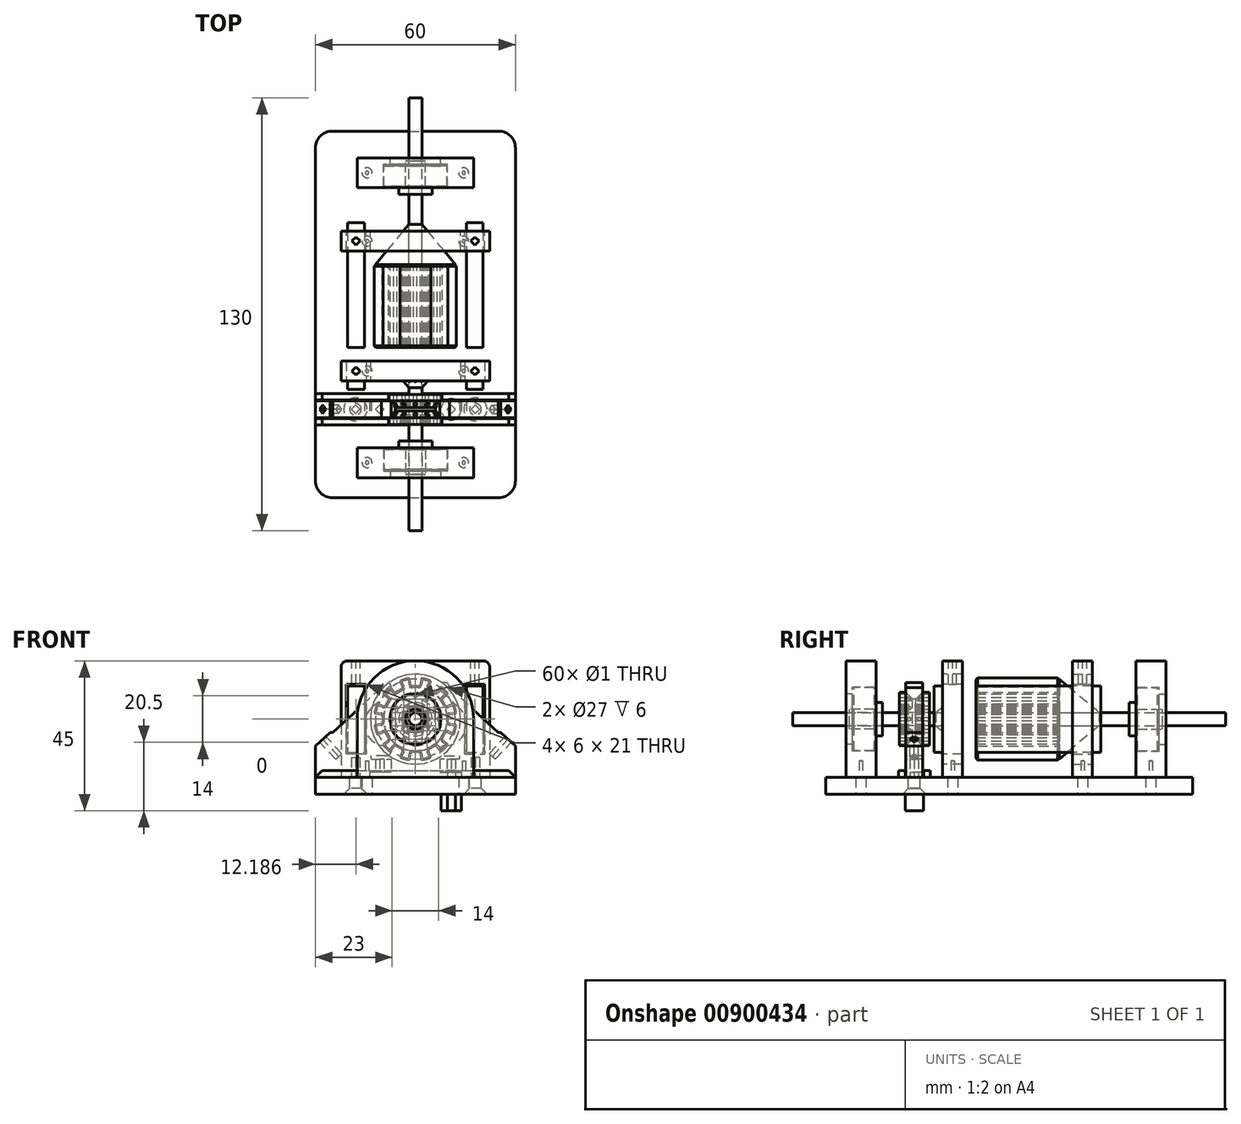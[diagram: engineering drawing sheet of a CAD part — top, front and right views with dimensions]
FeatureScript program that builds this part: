
annotation { "Feature Type Name" : "Feature", "Feature Type Description" : "" }
export const myFeature = defineFeature(function(context is Context, id is Id, definition is map)
    precondition{}
    {
        {
            var Q0;
            Q0=qCreatedBy(makeId("Front.planeOp"),FACE);
            var sketch = newSketch(context, id + "F0", { "sketchPlane" : qUnion([Q0])});
            skCircle(sketch, "E0", {"center": v(0, 0) * mm, "radius": 1.95 * mm});
            skSolve(sketch);
        }
        {
            var Q0;
            Q0=makeQuery(id+"F0.imprint","IMPRINT",FACE,{"disambiguationData":[TD([[makeQuery(id+"F0.imprint","IMPRINT",EDGE,{"derivedFrom":sQuery(id+"F0.wireOp",EDGE,"E0")}),1.0]])]});
            extrude(context, id + "F1", {"entities" : qUnion([Q0]), "depth" : 80 * mm, "offsetDistance" : 25 * mm, "hasSecondDirection" : true, "secondDirectionOppositeDirection" : true, "secondDirectionDepth" : 50 * mm});
        }
        {
            var Q0;
            Q0=qCreatedBy(makeId("Front.planeOp"),FACE);
            var sketch = newSketch(context, id + "F2", { "sketchPlane" : qUnion([Q0])});
            skCircle(sketch, "E1", {"center": v(0, 0) * mm, "radius": 15 * mm, "construction": true});
            skCircle(sketch, "E2", {"center": v(0, 0) * mm, "radius": 10 * mm, "construction": true});
            skLineSegment(sketch, "E3", {"start": v(0, 0) * mm, "end": v(15, 0) * mm, "construction": true});
            skLineSegment(sketch, "E4", {"start": v(0, 0) * mm, "end": v(9.91, 1.3) * mm, "construction": true});
            skLineSegment(sketch, "E5", {"start": v(0, 0) * mm, "end": v(9.91, -1.3) * mm, "construction": true});
            skLineSegment(sketch, "E6", {"start": v(11.89, 1.56) * mm, "end": v(10.35, 1.36) * mm});
            skLineSegment(sketch, "E7", {"start": v(9.91, 0.87) * mm, "end": v(9.91, -0.87) * mm});
            skLineSegment(sketch, "E8", {"start": v(10.35, -1.36) * mm, "end": v(11.89, -1.56) * mm});
            skPoint(sketch, "E9.visualSharp", {"position": v(9.91, 1.3) * mm});
            skArc(sketch, "E9.filletArc", {"start": v(10.35, 1.36) * mm, "mid": v(10.04, 1.2) * mm, "end": v(9.91, 0.87) * mm});
            skPoint(sketch, "E10.visualSharp", {"position": v(9.91, -1.3) * mm});
            skArc(sketch, "E10.filletArc", {"start": v(9.91, -0.87) * mm, "mid": v(10.04, -1.2) * mm, "end": v(10.35, -1.36) * mm});
            skArc(sketch, "E11.1.0", {"start": v(8.28, 6.35) * mm, "mid": v(8.1, 6.06) * mm, "end": v(8.15, 5.7) * mm});
            skLineSegment(sketch, "E11.1.1", {"start": v(9.51, 7.3) * mm, "end": v(8.28, 6.35) * mm});
            skLineSegment(sketch, "E11.1.2", {"start": v(8.15, 5.7) * mm, "end": v(9.02, 4.2) * mm});
            skArc(sketch, "E11.1.3", {"start": v(9.02, 4.2) * mm, "mid": v(9.3, 3.98) * mm, "end": v(9.64, 4) * mm});
            skLineSegment(sketch, "E11.1.4", {"start": v(9.64, 4) * mm, "end": v(11.08, 4.59) * mm});
            skArc(sketch, "E11.2.0", {"start": v(4, 9.64) * mm, "mid": v(3.98, 9.3) * mm, "end": v(4.2, 9.02) * mm});
            skLineSegment(sketch, "E11.2.1", {"start": v(4.59, 11.08) * mm, "end": v(4, 9.64) * mm});
            skLineSegment(sketch, "E11.2.2", {"start": v(4.2, 9.02) * mm, "end": v(5.7, 8.15) * mm});
            skArc(sketch, "E11.2.3", {"start": v(5.7, 8.15) * mm, "mid": v(6.06, 8.1) * mm, "end": v(6.35, 8.28) * mm});
            skLineSegment(sketch, "E11.2.4", {"start": v(6.35, 8.28) * mm, "end": v(7.3, 9.51) * mm});
            skLineSegment(sketch, "E12.4.3.0", {"start": v(-1.56, 11.89) * mm, "end": v(-1.36, 10.35) * mm});
            skLineSegment(sketch, "E12.7.3.0", {"start": v(-0.87, 9.91) * mm, "end": v(0.87, 9.91) * mm});
            skArc(sketch, "E12.10.3.0", {"start": v(0.87, 9.91) * mm, "mid": v(1.2, 10.04) * mm, "end": v(1.36, 10.35) * mm});
            skArc(sketch, "E12.13.3.0", {"start": v(-1.36, 10.35) * mm, "mid": v(-1.2, 10.04) * mm, "end": v(-0.87, 9.91) * mm});
            skLineSegment(sketch, "E12.14.3.0", {"start": v(1.36, 10.35) * mm, "end": v(1.56, 11.89) * mm});
            skLineSegment(sketch, "E12.4.4.0", {"start": v(-7.3, 9.51) * mm, "end": v(-6.35, 8.28) * mm});
            skLineSegment(sketch, "E12.7.4.0", {"start": v(-5.7, 8.15) * mm, "end": v(-4.2, 9.02) * mm});
            skArc(sketch, "E12.10.4.0", {"start": v(-4.2, 9.02) * mm, "mid": v(-3.98, 9.3) * mm, "end": v(-4, 9.64) * mm});
            skArc(sketch, "E12.13.4.0", {"start": v(-6.35, 8.28) * mm, "mid": v(-6.06, 8.1) * mm, "end": v(-5.7, 8.15) * mm});
            skLineSegment(sketch, "E12.14.4.0", {"start": v(-4, 9.64) * mm, "end": v(-4.59, 11.08) * mm});
            skLineSegment(sketch, "E12.4.5.0", {"start": v(-11.08, 4.59) * mm, "end": v(-9.64, 4) * mm});
            skLineSegment(sketch, "E12.7.5.0", {"start": v(-9.02, 4.2) * mm, "end": v(-8.15, 5.7) * mm});
            skArc(sketch, "E12.10.5.0", {"start": v(-8.15, 5.7) * mm, "mid": v(-8.1, 6.06) * mm, "end": v(-8.28, 6.35) * mm});
            skArc(sketch, "E12.13.5.0", {"start": v(-9.64, 4) * mm, "mid": v(-9.3, 3.98) * mm, "end": v(-9.02, 4.2) * mm});
            skLineSegment(sketch, "E12.14.5.0", {"start": v(-8.28, 6.35) * mm, "end": v(-9.51, 7.3) * mm});
            skLineSegment(sketch, "E12.4.6.0", {"start": v(-11.89, -1.56) * mm, "end": v(-10.35, -1.36) * mm});
            skLineSegment(sketch, "E12.7.6.0", {"start": v(-9.91, -0.87) * mm, "end": v(-9.91, 0.87) * mm});
            skArc(sketch, "E12.10.6.0", {"start": v(-9.91, 0.87) * mm, "mid": v(-10.04, 1.2) * mm, "end": v(-10.35, 1.36) * mm});
            skArc(sketch, "E12.13.6.0", {"start": v(-10.35, -1.36) * mm, "mid": v(-10.04, -1.2) * mm, "end": v(-9.91, -0.87) * mm});
            skLineSegment(sketch, "E12.14.6.0", {"start": v(-10.35, 1.36) * mm, "end": v(-11.89, 1.56) * mm});
            skLineSegment(sketch, "E12.4.7.0", {"start": v(-9.51, -7.3) * mm, "end": v(-8.28, -6.35) * mm});
            skLineSegment(sketch, "E12.7.7.0", {"start": v(-8.15, -5.7) * mm, "end": v(-9.02, -4.2) * mm});
            skArc(sketch, "E12.10.7.0", {"start": v(-9.02, -4.2) * mm, "mid": v(-9.3, -3.98) * mm, "end": v(-9.64, -4) * mm});
            skArc(sketch, "E12.13.7.0", {"start": v(-8.28, -6.35) * mm, "mid": v(-8.1, -6.06) * mm, "end": v(-8.15, -5.7) * mm});
            skLineSegment(sketch, "E12.14.7.0", {"start": v(-9.64, -4) * mm, "end": v(-11.08, -4.59) * mm});
            skLineSegment(sketch, "E12.4.8.0", {"start": v(-4.59, -11.08) * mm, "end": v(-4, -9.64) * mm});
            skLineSegment(sketch, "E12.7.8.0", {"start": v(-4.2, -9.02) * mm, "end": v(-5.7, -8.15) * mm});
            skArc(sketch, "E12.10.8.0", {"start": v(-5.7, -8.15) * mm, "mid": v(-6.06, -8.1) * mm, "end": v(-6.35, -8.28) * mm});
            skArc(sketch, "E12.13.8.0", {"start": v(-4, -9.64) * mm, "mid": v(-3.98, -9.3) * mm, "end": v(-4.2, -9.02) * mm});
            skLineSegment(sketch, "E12.14.8.0", {"start": v(-6.35, -8.28) * mm, "end": v(-7.3, -9.51) * mm});
            skLineSegment(sketch, "E12.4.9.0", {"start": v(1.56, -11.89) * mm, "end": v(1.36, -10.35) * mm});
            skLineSegment(sketch, "E12.7.9.0", {"start": v(0.87, -9.91) * mm, "end": v(-0.87, -9.91) * mm});
            skArc(sketch, "E12.10.9.0", {"start": v(-0.87, -9.91) * mm, "mid": v(-1.2, -10.04) * mm, "end": v(-1.36, -10.35) * mm});
            skArc(sketch, "E12.13.9.0", {"start": v(1.36, -10.35) * mm, "mid": v(1.2, -10.04) * mm, "end": v(0.87, -9.91) * mm});
            skLineSegment(sketch, "E12.14.9.0", {"start": v(-1.36, -10.35) * mm, "end": v(-1.56, -11.89) * mm});
            skLineSegment(sketch, "E12.4.10.0", {"start": v(7.3, -9.51) * mm, "end": v(6.35, -8.28) * mm});
            skLineSegment(sketch, "E12.7.10.0", {"start": v(5.7, -8.15) * mm, "end": v(4.2, -9.02) * mm});
            skArc(sketch, "E12.10.10.0", {"start": v(4.2, -9.02) * mm, "mid": v(3.98, -9.3) * mm, "end": v(4, -9.64) * mm});
            skArc(sketch, "E12.13.10.0", {"start": v(6.35, -8.28) * mm, "mid": v(6.06, -8.1) * mm, "end": v(5.7, -8.15) * mm});
            skLineSegment(sketch, "E12.14.10.0", {"start": v(4, -9.64) * mm, "end": v(4.59, -11.08) * mm});
            skLineSegment(sketch, "E12.4.11.0", {"start": v(11.08, -4.59) * mm, "end": v(9.64, -4) * mm});
            skLineSegment(sketch, "E12.7.11.0", {"start": v(9.02, -4.2) * mm, "end": v(8.15, -5.7) * mm});
            skArc(sketch, "E12.10.11.0", {"start": v(8.15, -5.7) * mm, "mid": v(8.1, -6.06) * mm, "end": v(8.28, -6.35) * mm});
            skArc(sketch, "E12.13.11.0", {"start": v(9.64, -4) * mm, "mid": v(9.3, -3.98) * mm, "end": v(9.02, -4.2) * mm});
            skLineSegment(sketch, "E12.14.11.0", {"start": v(8.28, -6.35) * mm, "end": v(9.51, -7.3) * mm});
            skArc(sketch, "E13", {"start": v(4.3, 11.74) * mm, "mid": v(3.24, 12.07) * mm, "end": v(2.15, 12.31) * mm});
            skArc(sketch, "E14.trimOffspring", {"start": v(9.6, 8.02) * mm, "mid": v(8.84, 8.84) * mm, "end": v(8.02, 9.6) * mm});
            skPoint(sketch, "E15.newPointA", {"position": v(7.61, 9.92) * mm});
            skArc(sketch, "E15.filletArc", {"start": v(8.02, 9.6) * mm, "mid": v(7.64, 9.7) * mm, "end": v(7.3, 9.51) * mm});
            skPoint(sketch, "E16.newPointB", {"position": v(9.92, 7.6) * mm});
            skArc(sketch, "E16.filletArc", {"start": v(9.51, 7.3) * mm, "mid": v(9.7, 7.64) * mm, "end": v(9.6, 8.02) * mm});
            skArc(sketch, "E17.trimOffspring", {"start": v(12.31, 2.15) * mm, "mid": v(12.07, 3.24) * mm, "end": v(11.74, 4.3) * mm});
            skArc(sketch, "E18.trimOffspring", {"start": v(11.74, -4.3) * mm, "mid": v(12.07, -3.24) * mm, "end": v(12.31, -2.15) * mm});
            skArc(sketch, "E19.trimOffspring", {"start": v(-2.15, 12.31) * mm, "mid": v(-3.24, 12.07) * mm, "end": v(-4.3, 11.74) * mm});
            skArc(sketch, "E20.trimOffspring", {"start": v(-8.02, 9.6) * mm, "mid": v(-8.84, 8.84) * mm, "end": v(-9.6, 8.02) * mm});
            skArc(sketch, "E21.trimOffspring", {"start": v(-11.74, 4.3) * mm, "mid": v(-12.07, 3.24) * mm, "end": v(-12.31, 2.15) * mm});
            skArc(sketch, "E22.trimOffspring", {"start": v(-12.31, -2.15) * mm, "mid": v(-12.07, -3.24) * mm, "end": v(-11.74, -4.3) * mm});
            skArc(sketch, "E23.trimOffspring", {"start": v(-9.6, -8.02) * mm, "mid": v(-8.84, -8.84) * mm, "end": v(-8.02, -9.6) * mm});
            skArc(sketch, "E24.trimOffspring", {"start": v(-4.3, -11.74) * mm, "mid": v(-3.24, -12.07) * mm, "end": v(-2.15, -12.31) * mm});
            skArc(sketch, "E25.trimOffspring", {"start": v(2.15, -12.31) * mm, "mid": v(3.24, -12.07) * mm, "end": v(4.3, -11.74) * mm});
            skArc(sketch, "E26.trimOffspring", {"start": v(8.02, -9.6) * mm, "mid": v(8.84, -8.84) * mm, "end": v(9.6, -8.02) * mm});
            skPoint(sketch, "E27.newPointB", {"position": v(4.78, 11.55) * mm});
            skArc(sketch, "E27.filletArc", {"start": v(4.59, 11.08) * mm, "mid": v(4.58, 11.47) * mm, "end": v(4.3, 11.74) * mm});
            skPoint(sketch, "E28.newPointB", {"position": v(1.63, 12.4) * mm});
            skArc(sketch, "E28.filletArc", {"start": v(2.15, 12.31) * mm, "mid": v(1.76, 12.22) * mm, "end": v(1.56, 11.89) * mm});
            skPoint(sketch, "E29.newPointB", {"position": v(-1.63, 12.4) * mm});
            skArc(sketch, "E29.filletArc", {"start": v(-1.56, 11.89) * mm, "mid": v(-1.76, 12.22) * mm, "end": v(-2.15, 12.31) * mm});
            skPoint(sketch, "E30.newPointB", {"position": v(-4.78, 11.55) * mm});
            skArc(sketch, "E30.filletArc", {"start": v(-4.3, 11.74) * mm, "mid": v(-4.58, 11.47) * mm, "end": v(-4.59, 11.08) * mm});
            skPoint(sketch, "E31.newPointB", {"position": v(-7.6, 9.92) * mm});
            skArc(sketch, "E31.filletArc", {"start": v(-7.3, 9.51) * mm, "mid": v(-7.64, 9.7) * mm, "end": v(-8.02, 9.6) * mm});
            skPoint(sketch, "E32.newPointB", {"position": v(-9.92, 7.61) * mm});
            skArc(sketch, "E32.filletArc", {"start": v(-9.6, 8.02) * mm, "mid": v(-9.7, 7.64) * mm, "end": v(-9.51, 7.3) * mm});
            skPoint(sketch, "E33.newPointB", {"position": v(-11.55, 4.78) * mm});
            skArc(sketch, "E33.filletArc", {"start": v(-11.08, 4.59) * mm, "mid": v(-11.47, 4.58) * mm, "end": v(-11.74, 4.3) * mm});
            skPoint(sketch, "E34.newPointB", {"position": v(-12.4, 1.63) * mm});
            skArc(sketch, "E34.filletArc", {"start": v(-12.31, 2.15) * mm, "mid": v(-12.22, 1.76) * mm, "end": v(-11.89, 1.56) * mm});
            skPoint(sketch, "E35.newPointA", {"position": v(-12.4, -1.63) * mm});
            skArc(sketch, "E35.filletArc", {"start": v(-11.89, -1.56) * mm, "mid": v(-12.22, -1.76) * mm, "end": v(-12.31, -2.15) * mm});
            skPoint(sketch, "E36.newPointA", {"position": v(-11.55, -4.78) * mm});
            skArc(sketch, "E36.filletArc", {"start": v(-11.74, -4.3) * mm, "mid": v(-11.47, -4.58) * mm, "end": v(-11.08, -4.59) * mm});
            skPoint(sketch, "E37.newPointA", {"position": v(-9.92, -7.6) * mm});
            skArc(sketch, "E37.filletArc", {"start": v(-9.51, -7.3) * mm, "mid": v(-9.7, -7.64) * mm, "end": v(-9.6, -8.02) * mm});
            skPoint(sketch, "E38.newPointA", {"position": v(-7.61, -9.92) * mm});
            skArc(sketch, "E38.filletArc", {"start": v(-8.02, -9.6) * mm, "mid": v(-7.64, -9.7) * mm, "end": v(-7.3, -9.51) * mm});
            skPoint(sketch, "E39.newPointA", {"position": v(-4.78, -11.55) * mm});
            skArc(sketch, "E39.filletArc", {"start": v(-4.59, -11.08) * mm, "mid": v(-4.58, -11.47) * mm, "end": v(-4.3, -11.74) * mm});
            skPoint(sketch, "E40.newPointA", {"position": v(-1.63, -12.4) * mm});
            skArc(sketch, "E40.filletArc", {"start": v(-2.15, -12.31) * mm, "mid": v(-1.76, -12.22) * mm, "end": v(-1.56, -11.89) * mm});
            skPoint(sketch, "E41.newPointA", {"position": v(1.63, -12.4) * mm});
            skArc(sketch, "E41.filletArc", {"start": v(1.56, -11.89) * mm, "mid": v(1.76, -12.22) * mm, "end": v(2.15, -12.31) * mm});
            skPoint(sketch, "E42.newPointA", {"position": v(4.78, -11.55) * mm});
            skArc(sketch, "E42.filletArc", {"start": v(4.3, -11.74) * mm, "mid": v(4.58, -11.47) * mm, "end": v(4.59, -11.08) * mm});
            skPoint(sketch, "E43.newPointA", {"position": v(7.6, -9.92) * mm});
            skArc(sketch, "E43.filletArc", {"start": v(7.3, -9.51) * mm, "mid": v(7.64, -9.7) * mm, "end": v(8.02, -9.6) * mm});
            skPoint(sketch, "E44.newPointA", {"position": v(9.92, -7.61) * mm});
            skArc(sketch, "E44.filletArc", {"start": v(9.6, -8.02) * mm, "mid": v(9.7, -7.64) * mm, "end": v(9.51, -7.3) * mm});
            skPoint(sketch, "E45.newPointB", {"position": v(11.55, -4.78) * mm});
            skArc(sketch, "E45.filletArc", {"start": v(11.08, -4.59) * mm, "mid": v(11.47, -4.58) * mm, "end": v(11.74, -4.3) * mm});
            skPoint(sketch, "E46.newPointA", {"position": v(12.4, -1.63) * mm});
            skArc(sketch, "E46.filletArc", {"start": v(12.31, -2.15) * mm, "mid": v(12.22, -1.76) * mm, "end": v(11.89, -1.56) * mm});
            skPoint(sketch, "E47.newPointA", {"position": v(12.4, 1.63) * mm});
            skArc(sketch, "E47.filletArc", {"start": v(11.89, 1.56) * mm, "mid": v(12.22, 1.76) * mm, "end": v(12.31, 2.15) * mm});
            skPoint(sketch, "E48.newPointB", {"position": v(11.55, 4.78) * mm});
            skArc(sketch, "E48.filletArc", {"start": v(11.74, 4.3) * mm, "mid": v(11.47, 4.58) * mm, "end": v(11.08, 4.59) * mm});
            skCircle(sketch, "E49", {"center": v(0, 0) * mm, "radius": 2 * mm});
            skPoint(sketch, "E50.centerSnap0", {"position": v(7.5, 0) * mm});
            skSolve(sketch);
        }
        {
            var Q0;
            Q0=makeQuery(id+"F2.imprint","IMPRINT",FACE,{"disambiguationData":[TD([[makeQuery(id+"F2.imprint","IMPRINT",EDGE,{"derivedFrom":sQuery(id+"F2.wireOp",EDGE,"E6")}),-1.0]])]});
            extrude(context, id + "F3", {"entities" : qUnion([Q0]), "depth" : 25 * mm, "offsetDistance" : 25 * mm});
        }
        {
            var Q0;
            Q0=makeQuery(id+"F3.opExtrude","CAP_FACE",FACE,{"disambiguationData":[OSD([sQuery(id+"F2.wireOp",EDGE,"E6"),sQuery(id+"F2.wireOp",EDGE,"E7"),sQuery(id+"F2.wireOp",EDGE,"E8"),sQuery(id+"F2.wireOp",EDGE,"E9.filletArc"),sQuery(id+"F2.wireOp",EDGE,"E10.filletArc"),sQuery(id+"F2.wireOp",EDGE,"E11.1.0"),sQuery(id+"F2.wireOp",EDGE,"E11.1.1"),sQuery(id+"F2.wireOp",EDGE,"E11.1.2"),sQuery(id+"F2.wireOp",EDGE,"E11.1.3"),sQuery(id+"F2.wireOp",EDGE,"E11.1.4"),sQuery(id+"F2.wireOp",EDGE,"E11.2.0"),sQuery(id+"F2.wireOp",EDGE,"E11.2.1"),sQuery(id+"F2.wireOp",EDGE,"E11.2.2"),sQuery(id+"F2.wireOp",EDGE,"E11.2.3"),sQuery(id+"F2.wireOp",EDGE,"E11.2.4"),sQuery(id+"F2.wireOp",EDGE,"E12.4.3.0"),sQuery(id+"F2.wireOp",EDGE,"E12.7.3.0"),sQuery(id+"F2.wireOp",EDGE,"E12.10.3.0"),sQuery(id+"F2.wireOp",EDGE,"E12.13.3.0"),sQuery(id+"F2.wireOp",EDGE,"E12.14.3.0"),sQuery(id+"F2.wireOp",EDGE,"E12.4.4.0"),sQuery(id+"F2.wireOp",EDGE,"E12.7.4.0"),sQuery(id+"F2.wireOp",EDGE,"E12.10.4.0"),sQuery(id+"F2.wireOp",EDGE,"E12.13.4.0"),sQuery(id+"F2.wireOp",EDGE,"E12.14.4.0"),sQuery(id+"F2.wireOp",EDGE,"E12.4.5.0"),sQuery(id+"F2.wireOp",EDGE,"E12.7.5.0"),sQuery(id+"F2.wireOp",EDGE,"E12.10.5.0"),sQuery(id+"F2.wireOp",EDGE,"E12.13.5.0"),sQuery(id+"F2.wireOp",EDGE,"E12.14.5.0"),sQuery(id+"F2.wireOp",EDGE,"E12.4.6.0"),sQuery(id+"F2.wireOp",EDGE,"E12.7.6.0"),sQuery(id+"F2.wireOp",EDGE,"E12.10.6.0"),sQuery(id+"F2.wireOp",EDGE,"E12.13.6.0"),sQuery(id+"F2.wireOp",EDGE,"E12.14.6.0"),sQuery(id+"F2.wireOp",EDGE,"E12.4.7.0"),sQuery(id+"F2.wireOp",EDGE,"E12.7.7.0"),sQuery(id+"F2.wireOp",EDGE,"E12.10.7.0"),sQuery(id+"F2.wireOp",EDGE,"E12.13.7.0"),sQuery(id+"F2.wireOp",EDGE,"E12.14.7.0"),sQuery(id+"F2.wireOp",EDGE,"E12.4.8.0"),sQuery(id+"F2.wireOp",EDGE,"E12.7.8.0"),sQuery(id+"F2.wireOp",EDGE,"E12.10.8.0"),sQuery(id+"F2.wireOp",EDGE,"E12.13.8.0"),sQuery(id+"F2.wireOp",EDGE,"E12.14.8.0"),sQuery(id+"F2.wireOp",EDGE,"E12.4.9.0"),sQuery(id+"F2.wireOp",EDGE,"E12.7.9.0"),sQuery(id+"F2.wireOp",EDGE,"E12.10.9.0"),sQuery(id+"F2.wireOp",EDGE,"E12.13.9.0"),sQuery(id+"F2.wireOp",EDGE,"E12.14.9.0"),sQuery(id+"F2.wireOp",EDGE,"E12.4.10.0"),sQuery(id+"F2.wireOp",EDGE,"E12.7.10.0"),sQuery(id+"F2.wireOp",EDGE,"E12.10.10.0"),sQuery(id+"F2.wireOp",EDGE,"E12.13.10.0"),sQuery(id+"F2.wireOp",EDGE,"E12.14.10.0"),sQuery(id+"F2.wireOp",EDGE,"E12.4.11.0"),sQuery(id+"F2.wireOp",EDGE,"E12.7.11.0"),sQuery(id+"F2.wireOp",EDGE,"E12.10.11.0"),sQuery(id+"F2.wireOp",EDGE,"E12.13.11.0"),sQuery(id+"F2.wireOp",EDGE,"E12.14.11.0"),sQuery(id+"F2.wireOp",EDGE,"E13"),sQuery(id+"F2.wireOp",EDGE,"E14.trimOffspring"),sQuery(id+"F2.wireOp",EDGE,"E15.filletArc"),sQuery(id+"F2.wireOp",EDGE,"E16.filletArc"),sQuery(id+"F2.wireOp",EDGE,"E17.trimOffspring"),sQuery(id+"F2.wireOp",EDGE,"E18.trimOffspring"),sQuery(id+"F2.wireOp",EDGE,"E19.trimOffspring"),sQuery(id+"F2.wireOp",EDGE,"E20.trimOffspring"),sQuery(id+"F2.wireOp",EDGE,"E21.trimOffspring"),sQuery(id+"F2.wireOp",EDGE,"E22.trimOffspring"),sQuery(id+"F2.wireOp",EDGE,"E23.trimOffspring"),sQuery(id+"F2.wireOp",EDGE,"E24.trimOffspring"),sQuery(id+"F2.wireOp",EDGE,"E25.trimOffspring"),sQuery(id+"F2.wireOp",EDGE,"E26.trimOffspring"),sQuery(id+"F2.wireOp",EDGE,"E27.filletArc"),sQuery(id+"F2.wireOp",EDGE,"E28.filletArc"),sQuery(id+"F2.wireOp",EDGE,"E29.filletArc"),sQuery(id+"F2.wireOp",EDGE,"E30.filletArc"),sQuery(id+"F2.wireOp",EDGE,"E31.filletArc"),sQuery(id+"F2.wireOp",EDGE,"E32.filletArc"),sQuery(id+"F2.wireOp",EDGE,"E33.filletArc"),sQuery(id+"F2.wireOp",EDGE,"E34.filletArc"),sQuery(id+"F2.wireOp",EDGE,"E35.filletArc"),sQuery(id+"F2.wireOp",EDGE,"E36.filletArc"),sQuery(id+"F2.wireOp",EDGE,"E37.filletArc"),sQuery(id+"F2.wireOp",EDGE,"E38.filletArc"),sQuery(id+"F2.wireOp",EDGE,"E39.filletArc"),sQuery(id+"F2.wireOp",EDGE,"E40.filletArc"),sQuery(id+"F2.wireOp",EDGE,"E41.filletArc"),sQuery(id+"F2.wireOp",EDGE,"E42.filletArc"),sQuery(id+"F2.wireOp",EDGE,"E43.filletArc"),sQuery(id+"F2.wireOp",EDGE,"E44.filletArc"),sQuery(id+"F2.wireOp",EDGE,"E45.filletArc"),sQuery(id+"F2.wireOp",EDGE,"E46.filletArc"),sQuery(id+"F2.wireOp",EDGE,"E47.filletArc"),sQuery(id+"F2.wireOp",EDGE,"E48.filletArc"),sQuery(id+"F2.wireOp",EDGE,"E49")])],"isStart":false});
            chamfer(context, id + "F4", {"entities" : qUnion([Q0]), "width" : 0.5 * mm, "tangentPropagation" : true});
        }
        {
            var Q0;
            Q0=makeQuery(id+"F3.opExtrude","CAP_FACE",FACE,{"disambiguationData":[OSD([sQuery(id+"F2.wireOp",EDGE,"E6"),sQuery(id+"F2.wireOp",EDGE,"E7"),sQuery(id+"F2.wireOp",EDGE,"E8"),sQuery(id+"F2.wireOp",EDGE,"E9.filletArc"),sQuery(id+"F2.wireOp",EDGE,"E10.filletArc"),sQuery(id+"F2.wireOp",EDGE,"E11.1.0"),sQuery(id+"F2.wireOp",EDGE,"E11.1.1"),sQuery(id+"F2.wireOp",EDGE,"E11.1.2"),sQuery(id+"F2.wireOp",EDGE,"E11.1.3"),sQuery(id+"F2.wireOp",EDGE,"E11.1.4"),sQuery(id+"F2.wireOp",EDGE,"E11.2.0"),sQuery(id+"F2.wireOp",EDGE,"E11.2.1"),sQuery(id+"F2.wireOp",EDGE,"E11.2.2"),sQuery(id+"F2.wireOp",EDGE,"E11.2.3"),sQuery(id+"F2.wireOp",EDGE,"E11.2.4"),sQuery(id+"F2.wireOp",EDGE,"E12.4.3.0"),sQuery(id+"F2.wireOp",EDGE,"E12.7.3.0"),sQuery(id+"F2.wireOp",EDGE,"E12.10.3.0"),sQuery(id+"F2.wireOp",EDGE,"E12.13.3.0"),sQuery(id+"F2.wireOp",EDGE,"E12.14.3.0"),sQuery(id+"F2.wireOp",EDGE,"E12.4.4.0"),sQuery(id+"F2.wireOp",EDGE,"E12.7.4.0"),sQuery(id+"F2.wireOp",EDGE,"E12.10.4.0"),sQuery(id+"F2.wireOp",EDGE,"E12.13.4.0"),sQuery(id+"F2.wireOp",EDGE,"E12.14.4.0"),sQuery(id+"F2.wireOp",EDGE,"E12.4.5.0"),sQuery(id+"F2.wireOp",EDGE,"E12.7.5.0"),sQuery(id+"F2.wireOp",EDGE,"E12.10.5.0"),sQuery(id+"F2.wireOp",EDGE,"E12.13.5.0"),sQuery(id+"F2.wireOp",EDGE,"E12.14.5.0"),sQuery(id+"F2.wireOp",EDGE,"E12.4.6.0"),sQuery(id+"F2.wireOp",EDGE,"E12.7.6.0"),sQuery(id+"F2.wireOp",EDGE,"E12.10.6.0"),sQuery(id+"F2.wireOp",EDGE,"E12.13.6.0"),sQuery(id+"F2.wireOp",EDGE,"E12.14.6.0"),sQuery(id+"F2.wireOp",EDGE,"E12.4.7.0"),sQuery(id+"F2.wireOp",EDGE,"E12.7.7.0"),sQuery(id+"F2.wireOp",EDGE,"E12.10.7.0"),sQuery(id+"F2.wireOp",EDGE,"E12.13.7.0"),sQuery(id+"F2.wireOp",EDGE,"E12.14.7.0"),sQuery(id+"F2.wireOp",EDGE,"E12.4.8.0"),sQuery(id+"F2.wireOp",EDGE,"E12.7.8.0"),sQuery(id+"F2.wireOp",EDGE,"E12.10.8.0"),sQuery(id+"F2.wireOp",EDGE,"E12.13.8.0"),sQuery(id+"F2.wireOp",EDGE,"E12.14.8.0"),sQuery(id+"F2.wireOp",EDGE,"E12.4.9.0"),sQuery(id+"F2.wireOp",EDGE,"E12.7.9.0"),sQuery(id+"F2.wireOp",EDGE,"E12.10.9.0"),sQuery(id+"F2.wireOp",EDGE,"E12.13.9.0"),sQuery(id+"F2.wireOp",EDGE,"E12.14.9.0"),sQuery(id+"F2.wireOp",EDGE,"E12.4.10.0"),sQuery(id+"F2.wireOp",EDGE,"E12.7.10.0"),sQuery(id+"F2.wireOp",EDGE,"E12.10.10.0"),sQuery(id+"F2.wireOp",EDGE,"E12.13.10.0"),sQuery(id+"F2.wireOp",EDGE,"E12.14.10.0"),sQuery(id+"F2.wireOp",EDGE,"E12.4.11.0"),sQuery(id+"F2.wireOp",EDGE,"E12.7.11.0"),sQuery(id+"F2.wireOp",EDGE,"E12.10.11.0"),sQuery(id+"F2.wireOp",EDGE,"E12.13.11.0"),sQuery(id+"F2.wireOp",EDGE,"E12.14.11.0"),sQuery(id+"F2.wireOp",EDGE,"E13"),sQuery(id+"F2.wireOp",EDGE,"E14.trimOffspring"),sQuery(id+"F2.wireOp",EDGE,"E15.filletArc"),sQuery(id+"F2.wireOp",EDGE,"E16.filletArc"),sQuery(id+"F2.wireOp",EDGE,"E17.trimOffspring"),sQuery(id+"F2.wireOp",EDGE,"E18.trimOffspring"),sQuery(id+"F2.wireOp",EDGE,"E19.trimOffspring"),sQuery(id+"F2.wireOp",EDGE,"E20.trimOffspring"),sQuery(id+"F2.wireOp",EDGE,"E21.trimOffspring"),sQuery(id+"F2.wireOp",EDGE,"E22.trimOffspring"),sQuery(id+"F2.wireOp",EDGE,"E23.trimOffspring"),sQuery(id+"F2.wireOp",EDGE,"E24.trimOffspring"),sQuery(id+"F2.wireOp",EDGE,"E25.trimOffspring"),sQuery(id+"F2.wireOp",EDGE,"E26.trimOffspring"),sQuery(id+"F2.wireOp",EDGE,"E27.filletArc"),sQuery(id+"F2.wireOp",EDGE,"E28.filletArc"),sQuery(id+"F2.wireOp",EDGE,"E29.filletArc"),sQuery(id+"F2.wireOp",EDGE,"E30.filletArc"),sQuery(id+"F2.wireOp",EDGE,"E31.filletArc"),sQuery(id+"F2.wireOp",EDGE,"E32.filletArc"),sQuery(id+"F2.wireOp",EDGE,"E33.filletArc"),sQuery(id+"F2.wireOp",EDGE,"E34.filletArc"),sQuery(id+"F2.wireOp",EDGE,"E35.filletArc"),sQuery(id+"F2.wireOp",EDGE,"E36.filletArc"),sQuery(id+"F2.wireOp",EDGE,"E37.filletArc"),sQuery(id+"F2.wireOp",EDGE,"E38.filletArc"),sQuery(id+"F2.wireOp",EDGE,"E39.filletArc"),sQuery(id+"F2.wireOp",EDGE,"E40.filletArc"),sQuery(id+"F2.wireOp",EDGE,"E41.filletArc"),sQuery(id+"F2.wireOp",EDGE,"E42.filletArc"),sQuery(id+"F2.wireOp",EDGE,"E43.filletArc"),sQuery(id+"F2.wireOp",EDGE,"E44.filletArc"),sQuery(id+"F2.wireOp",EDGE,"E45.filletArc"),sQuery(id+"F2.wireOp",EDGE,"E46.filletArc"),sQuery(id+"F2.wireOp",EDGE,"E47.filletArc"),sQuery(id+"F2.wireOp",EDGE,"E48.filletArc"),sQuery(id+"F2.wireOp",EDGE,"E49")])],"isStart":true});
            chamfer(context, id + "F5", {"entities" : qUnion([Q0]), "width" : 0.5 * mm, "tangentPropagation" : true});
        }
        {
            var Q0;
            Q0=qCreatedBy(makeId("Top.planeOp"),FACE);
            var sketch = newSketch(context, id + "F6", { "sketchPlane" : qUnion([Q0])});
            skLineSegment(sketch, "E51", {"start": v(2, 0) * mm, "end": v(12, 0) * mm});
            skLineSegment(sketch, "E52", {"start": v(12, 0) * mm, "end": v(2, 12) * mm});
            skLineSegment(sketch, "E53", {"start": v(2, 12) * mm, "end": v(2, 0) * mm});
            skLineSegment(sketch, "E54", {"start": v(0, 0) * mm, "end": v(-30, 0) * mm, "construction": true});
            skLineSegment(sketch, "E55", {"start": v(-30, -25) * mm, "end": v(0, -25) * mm, "construction": true});
            skLineSegment(sketch, "E56", {"start": v(-30, 0) * mm, "end": v(-30, -25) * mm, "construction": true});
            skLineSegment(sketch, "E57", {"start": v(-30, -12.5) * mm, "end": v(0, -12.5) * mm, "construction": true});
            skLineSegment(sketch, "E58.MirrorCS", {"start": v(2, -25) * mm, "end": v(12, -25) * mm});
            skLineSegment(sketch, "E59.MirrorCS", {"start": v(2, -37) * mm, "end": v(2, -25) * mm});
            skLineSegment(sketch, "E60.MirrorCS", {"start": v(12, -25) * mm, "end": v(2, -37) * mm});
            skLineSegment(sketch, "E61", {"start": v(0, 0) * mm, "end": v(0, -25) * mm, "construction": true});
            skSolve(sketch);
        }
        {
            var Q0;
            Q0=makeQuery(id+"F6.imprint","IMPRINT",FACE,{"disambiguationData":[TD([[makeQuery(id+"F6.imprint","IMPRINT",EDGE,{"derivedFrom":sQuery(id+"F6.wireOp",EDGE,"E51")}),1.0]])]});
            var Q1;
            Q1=makeQuery(id+"F6.imprint","IMPRINT",FACE,{"disambiguationData":[TD([[makeQuery(id+"F6.imprint","IMPRINT",EDGE,{"derivedFrom":sQuery(id+"F6.wireOp",EDGE,"E58.MirrorCS")}),-1.0]])]});
            var Q2;
            Q2=sQuery(id+"F6.wireOp",EDGE,"E61");
            revolve(context, id + "F7", {"surfaceOperationType" : NewSurfaceOperationType.NEW, "entities" : qUnion([Q0, Q1]), "axis" : qUnion([Q2]), "revolveType" : RevolveType.FULL});
        }
        {
            var Q0;
            Q0=qCreatedBy(makeId("Front.planeOp"),FACE);
            var sketch = newSketch(context, id + "F8", { "sketchPlane" : qUnion([Q0])});
            skCircle(sketch, "E62", {"center": v(7, 0) * mm, "radius": 0.5 * mm});
            skCircle(sketch, "E63", {"center": v(4, 0) * mm, "radius": 0.5 * mm});
            skCircle(sketch, "E64.1.0", {"center": v(3.46, 2) * mm, "radius": 0.5 * mm});
            skCircle(sketch, "E64.1.1", {"center": v(6.06, 3.5) * mm, "radius": 0.5 * mm});
            skCircle(sketch, "E64.2.0", {"center": v(2, 3.46) * mm, "radius": 0.5 * mm});
            skCircle(sketch, "E64.2.1", {"center": v(3.5, 6.06) * mm, "radius": 0.5 * mm});
            skPoint(sketch, "E64.center", {"position": v(0, 0) * mm});
            skCircle(sketch, "E65.1.3.0", {"center": v(0, 4) * mm, "radius": 0.5 * mm});
            skCircle(sketch, "E65.2.3.0", {"center": v(0, 7) * mm, "radius": 0.5 * mm});
            skCircle(sketch, "E65.1.4.0", {"center": v(-2, 3.46) * mm, "radius": 0.5 * mm});
            skCircle(sketch, "E65.2.4.0", {"center": v(-3.5, 6.06) * mm, "radius": 0.5 * mm});
            skCircle(sketch, "E65.1.5.0", {"center": v(-3.46, 2) * mm, "radius": 0.5 * mm});
            skCircle(sketch, "E65.2.5.0", {"center": v(-6.06, 3.5) * mm, "radius": 0.5 * mm});
            skCircle(sketch, "E65.1.6.0", {"center": v(-4, 0) * mm, "radius": 0.5 * mm});
            skCircle(sketch, "E65.2.6.0", {"center": v(-7, 0) * mm, "radius": 0.5 * mm});
            skCircle(sketch, "E65.1.7.0", {"center": v(-3.46, -2) * mm, "radius": 0.5 * mm});
            skCircle(sketch, "E65.2.7.0", {"center": v(-6.06, -3.5) * mm, "radius": 0.5 * mm});
            skCircle(sketch, "E65.1.8.0", {"center": v(-2, -3.46) * mm, "radius": 0.5 * mm});
            skCircle(sketch, "E65.2.8.0", {"center": v(-3.5, -6.06) * mm, "radius": 0.5 * mm});
            skCircle(sketch, "E65.1.9.0", {"center": v(0, -4) * mm, "radius": 0.5 * mm});
            skCircle(sketch, "E65.2.9.0", {"center": v(0, -7) * mm, "radius": 0.5 * mm});
            skCircle(sketch, "E65.1.10.0", {"center": v(2, -3.46) * mm, "radius": 0.5 * mm});
            skCircle(sketch, "E65.2.10.0", {"center": v(3.5, -6.06) * mm, "radius": 0.5 * mm});
            skCircle(sketch, "E65.1.11.0", {"center": v(3.46, -2) * mm, "radius": 0.5 * mm});
            skCircle(sketch, "E65.2.11.0", {"center": v(6.06, -3.5) * mm, "radius": 0.5 * mm});
            skSolve(sketch);
        }
        {
            var Q0;
            Q0=qCreatedBy(makeId("Top.planeOp"),FACE);
            var sketch = newSketch(context, id + "F9", { "sketchPlane" : qUnion([Q0])});
            skLineSegment(sketch, "E66", {"start": v(2, -39) * mm, "end": v(8, -39) * mm});
            skLineSegment(sketch, "E67", {"start": v(8, -39) * mm, "end": v(8, -41) * mm});
            skLineSegment(sketch, "E68", {"start": v(8, -41) * mm, "end": v(6, -43) * mm});
            skLineSegment(sketch, "E69", {"start": v(6, -43) * mm, "end": v(6, -44) * mm});
            skLineSegment(sketch, "E70", {"start": v(6, -44) * mm, "end": v(8, -46) * mm});
            skLineSegment(sketch, "E71", {"start": v(8, -46) * mm, "end": v(8, -48) * mm});
            skLineSegment(sketch, "E72", {"start": v(8, -48) * mm, "end": v(2, -48) * mm});
            skLineSegment(sketch, "E73", {"start": v(2, -48) * mm, "end": v(2, -39) * mm});
            skLineSegment(sketch, "E74", {"start": v(0, -53.33) * mm, "end": v(0, 0) * mm, "construction": true});
            skSolve(sketch);
        }
        {
            var Q0;
            Q0=makeQuery(id+"F9.imprint","IMPRINT",FACE,{"disambiguationData":[TD([[makeQuery(id+"F9.imprint","IMPRINT",EDGE,{"derivedFrom":sQuery(id+"F9.wireOp",EDGE,"E66")}),-1.0]])]});
            var Q1;
            Q1=sQuery(id+"F9.wireOp",EDGE,"E74");
            revolve(context, id + "F10", {"surfaceOperationType" : NewSurfaceOperationType.NEW, "entities" : qUnion([Q0]), "axis" : qUnion([Q1]), "revolveType" : RevolveType.FULL});
        }
        {
            var Q0;
            Q0=makeQuery(id+"F8.imprint","IMPRINT",FACE,{"disambiguationData":[TD([[makeQuery(id+"F8.imprint","IMPRINT",EDGE,{"derivedFrom":sQuery(id+"F8.wireOp",EDGE,"E65.2.3.0")}),1.0]])]});
            var Q1;
            Q1=makeQuery(id+"F8.imprint","IMPRINT",FACE,{"disambiguationData":[TD([[makeQuery(id+"F8.imprint","IMPRINT",EDGE,{"derivedFrom":sQuery(id+"F8.wireOp",EDGE,"E64.2.1")}),1.0]])]});
            var Q2;
            Q2=makeQuery(id+"F8.imprint","IMPRINT",FACE,{"disambiguationData":[TD([[makeQuery(id+"F8.imprint","IMPRINT",EDGE,{"derivedFrom":sQuery(id+"F8.wireOp",EDGE,"E64.1.1")}),1.0]])]});
            var Q3;
            Q3=makeQuery(id+"F8.imprint","IMPRINT",FACE,{"disambiguationData":[TD([[makeQuery(id+"F8.imprint","IMPRINT",EDGE,{"derivedFrom":sQuery(id+"F8.wireOp",EDGE,"E62")}),1.0]])]});
            var Q4;
            Q4=makeQuery(id+"F8.imprint","IMPRINT",FACE,{"disambiguationData":[TD([[makeQuery(id+"F8.imprint","IMPRINT",EDGE,{"derivedFrom":sQuery(id+"F8.wireOp",EDGE,"E65.2.11.0")}),1.0]])]});
            var Q5;
            Q5=makeQuery(id+"F8.imprint","IMPRINT",FACE,{"disambiguationData":[TD([[makeQuery(id+"F8.imprint","IMPRINT",EDGE,{"derivedFrom":sQuery(id+"F8.wireOp",EDGE,"E65.2.4.0")}),1.0]])]});
            var Q6;
            Q6=makeQuery(id+"F8.imprint","IMPRINT",FACE,{"disambiguationData":[TD([[makeQuery(id+"F8.imprint","IMPRINT",EDGE,{"derivedFrom":sQuery(id+"F8.wireOp",EDGE,"E65.1.10.0")}),1.0]])]});
            var Q7;
            Q7=makeQuery(id+"F8.imprint","IMPRINT",FACE,{"disambiguationData":[TD([[makeQuery(id+"F8.imprint","IMPRINT",EDGE,{"derivedFrom":sQuery(id+"F8.wireOp",EDGE,"E65.2.6.0")}),1.0]])]});
            var Q8;
            Q8=makeQuery(id+"F8.imprint","IMPRINT",FACE,{"disambiguationData":[TD([[makeQuery(id+"F8.imprint","IMPRINT",EDGE,{"derivedFrom":sQuery(id+"F8.wireOp",EDGE,"E65.2.7.0")}),1.0]])]});
            var Q9;
            Q9=makeQuery(id+"F8.imprint","IMPRINT",FACE,{"disambiguationData":[TD([[makeQuery(id+"F8.imprint","IMPRINT",EDGE,{"derivedFrom":sQuery(id+"F8.wireOp",EDGE,"E65.2.8.0")}),1.0]])]});
            var Q10;
            Q10=makeQuery(id+"F8.imprint","IMPRINT",FACE,{"disambiguationData":[TD([[makeQuery(id+"F8.imprint","IMPRINT",EDGE,{"derivedFrom":sQuery(id+"F8.wireOp",EDGE,"E64.1.0")}),1.0]])]});
            var Q11;
            Q11=makeQuery(id+"F8.imprint","IMPRINT",FACE,{"disambiguationData":[TD([[makeQuery(id+"F8.imprint","IMPRINT",EDGE,{"derivedFrom":sQuery(id+"F8.wireOp",EDGE,"E65.2.10.0")}),1.0]])]});
            var Q12;
            Q12=makeQuery(id+"F8.imprint","IMPRINT",FACE,{"disambiguationData":[TD([[makeQuery(id+"F8.imprint","IMPRINT",EDGE,{"derivedFrom":sQuery(id+"F8.wireOp",EDGE,"E65.1.11.0")}),1.0]])]});
            var Q13;
            Q13=makeQuery(id+"F8.imprint","IMPRINT",FACE,{"disambiguationData":[TD([[makeQuery(id+"F8.imprint","IMPRINT",EDGE,{"derivedFrom":sQuery(id+"F8.wireOp",EDGE,"E64.2.0")}),1.0]])]});
            var Q14;
            Q14=makeQuery(id+"F8.imprint","IMPRINT",FACE,{"disambiguationData":[TD([[makeQuery(id+"F8.imprint","IMPRINT",EDGE,{"derivedFrom":sQuery(id+"F8.wireOp",EDGE,"E65.1.6.0")}),1.0]])]});
            var Q15;
            Q15=makeQuery(id+"F8.imprint","IMPRINT",FACE,{"disambiguationData":[TD([[makeQuery(id+"F8.imprint","IMPRINT",EDGE,{"derivedFrom":sQuery(id+"F8.wireOp",EDGE,"E65.1.4.0")}),1.0]])]});
            var Q16;
            Q16=makeQuery(id+"F8.imprint","IMPRINT",FACE,{"disambiguationData":[TD([[makeQuery(id+"F8.imprint","IMPRINT",EDGE,{"derivedFrom":sQuery(id+"F8.wireOp",EDGE,"E65.1.5.0")}),1.0]])]});
            var Q17;
            Q17=makeQuery(id+"F8.imprint","IMPRINT",FACE,{"disambiguationData":[TD([[makeQuery(id+"F8.imprint","IMPRINT",EDGE,{"derivedFrom":sQuery(id+"F8.wireOp",EDGE,"E65.1.7.0")}),1.0]])]});
            var Q18;
            Q18=makeQuery(id+"F8.imprint","IMPRINT",FACE,{"disambiguationData":[TD([[makeQuery(id+"F8.imprint","IMPRINT",EDGE,{"derivedFrom":sQuery(id+"F8.wireOp",EDGE,"E65.1.9.0")}),1.0]])]});
            var Q19;
            Q19=makeQuery(id+"F8.imprint","IMPRINT",FACE,{"disambiguationData":[TD([[makeQuery(id+"F8.imprint","IMPRINT",EDGE,{"derivedFrom":sQuery(id+"F8.wireOp",EDGE,"E65.1.8.0")}),1.0]])]});
            var Q20;
            Q20=makeQuery(id+"F8.imprint","IMPRINT",FACE,{"disambiguationData":[TD([[makeQuery(id+"F8.imprint","IMPRINT",EDGE,{"derivedFrom":sQuery(id+"F8.wireOp",EDGE,"E65.2.9.0")}),1.0]])]});
            var Q21;
            Q21=makeQuery(id+"F8.imprint","IMPRINT",FACE,{"disambiguationData":[TD([[makeQuery(id+"F8.imprint","IMPRINT",EDGE,{"derivedFrom":sQuery(id+"F8.wireOp",EDGE,"E65.2.5.0")}),1.0]])]});
            var Q22;
            Q22=makeQuery(id+"F8.imprint","IMPRINT",FACE,{"disambiguationData":[TD([[makeQuery(id+"F8.imprint","IMPRINT",EDGE,{"derivedFrom":sQuery(id+"F8.wireOp",EDGE,"E63")}),1.0]])]});
            var Q23;
            Q23=makeQuery(id+"F8.imprint","IMPRINT",FACE,{"disambiguationData":[TD([[makeQuery(id+"F8.imprint","IMPRINT",EDGE,{"derivedFrom":sQuery(id+"F8.wireOp",EDGE,"E65.1.3.0")}),1.0]])]});
            extrude(context, id + "F11", {"entities" : qUnion([Q0, Q1, Q2, Q3, Q4, Q5, Q6, Q7, Q8, Q9, Q10, Q11, Q12, Q13, Q14, Q15, Q16, Q17, Q18, Q19, Q20, Q21, Q22, Q23]), "operationType" : NewBodyOperationType.REMOVE, "depth" : 50 * mm, "offsetDistance" : 25 * mm});
        }
        {
            var Q0;
            Q0=qCreatedBy(makeId("Top.planeOp"),FACE);
            var sketch = newSketch(context, id + "F12", { "sketchPlane" : qUnion([Q0])});
            skLineSegment(sketch, "E75", {"start": v(2, -53) * mm, "end": v(2, -63) * mm});
            skLineSegment(sketch, "E76", {"start": v(2, -63) * mm, "end": v(3, -63) * mm});
            skLineSegment(sketch, "E77", {"start": v(3, -63) * mm, "end": v(3, -55) * mm});
            skLineSegment(sketch, "E78", {"start": v(3, -55) * mm, "end": v(5, -55) * mm});
            skLineSegment(sketch, "E79", {"start": v(5, -55) * mm, "end": v(5, -53) * mm});
            skLineSegment(sketch, "E80", {"start": v(5, -53) * mm, "end": v(3, -53) * mm});
            skLineSegment(sketch, "E81", {"start": v(3, -53) * mm, "end": v(3, -53) * mm});
            skLineSegment(sketch, "E82", {"start": v(3, -53) * mm, "end": v(2, -53) * mm});
            skLineSegment(sketch, "E83", {"start": v(3, -53) * mm, "end": v(3, -55) * mm, "construction": true});
            skLineSegment(sketch, "E84.bottom", {"start": v(3, -55.5) * mm, "end": v(9.5, -55.5) * mm});
            skLineSegment(sketch, "E84.top", {"start": v(3, -61.5) * mm, "end": v(9.5, -61.5) * mm});
            skLineSegment(sketch, "E84.left", {"start": v(3, -55.5) * mm, "end": v(3, -61.5) * mm});
            skLineSegment(sketch, "E84.right", {"start": v(9.5, -55.5) * mm, "end": v(9.5, -61.5) * mm});
            skLineSegment(sketch, "E85.bottom", {"start": v(9.6, -55) * mm, "end": v(16.6, -55) * mm});
            skLineSegment(sketch, "E85.left", {"start": v(9.6, -55) * mm, "end": v(9.6, -62) * mm});
            skLineSegment(sketch, "E85.right", {"start": v(16.6, -55) * mm, "end": v(16.6, -64) * mm});
            skLineSegment(sketch, "E86", {"start": v(5, -55) * mm, "end": v(9.6, -55) * mm, "construction": true});
            skLineSegment(sketch, "E87.bottom", {"start": v(9.6, -62) * mm, "end": v(7.6, -62) * mm});
            skLineSegment(sketch, "E87.right", {"start": v(7.6, -62) * mm, "end": v(7.6, -64) * mm});
            skLineSegment(sketch, "E88", {"start": v(7.6, -64) * mm, "end": v(16.6, -64) * mm});
            skSolve(sketch);
        }
        {
            var Q0;
            Q0=makeQuery(id+"F12.imprint","IMPRINT",FACE,{"disambiguationData":[TD([[makeQuery(id+"F12.imprint","IMPRINT",EDGE,{"derivedFrom":sQuery(id+"F12.wireOp",EDGE,"E75")}),1.0]])]});
            var Q1;
            Q1=makeQuery(id+"F1.opExtrude","SWEPT_FACE",FACE,{"disambiguationData":[OSD([sQuery(id+"F0.wireOp",EDGE,"E0")])]});
            revolve(context, id + "F13", {"surfaceOperationType" : NewSurfaceOperationType.NEW, "entities" : qUnion([Q0]), "axis" : qUnion([Q1]), "revolveType" : RevolveType.FULL});
        }
        {
            var Q0;
            Q0=makeQuery(id+"F12.imprint","IMPRINT",FACE,{"disambiguationData":[TD([[makeQuery(id+"F12.imprint","IMPRINT",EDGE,{"derivedFrom":sQuery(id+"F12.wireOp",EDGE,"E84.bottom")}),-1.0]])]});
            var Q1;
            Q1=makeQuery(id+"F1.opExtrude","SWEPT_FACE",FACE,{"disambiguationData":[OSD([sQuery(id+"F0.wireOp",EDGE,"E0")])]});
            revolve(context, id + "F14", {"surfaceOperationType" : NewSurfaceOperationType.NEW, "entities" : qUnion([Q0]), "axis" : qUnion([Q1]), "revolveType" : RevolveType.FULL});
        }
        {
            var Q0;
            Q0=makeQuery(id+"F12.imprint","IMPRINT",FACE,{"disambiguationData":[TD([[makeQuery(id+"F12.imprint","IMPRINT",EDGE,{"derivedFrom":sQuery(id+"F12.wireOp",EDGE,"E85.bottom")}),-1.0]])]});
            var Q1;
            Q1=makeQuery(id+"F1.opExtrude","SWEPT_FACE",FACE,{"disambiguationData":[OSD([sQuery(id+"F0.wireOp",EDGE,"E0")])]});
            revolve(context, id + "F15", {"surfaceOperationType" : NewSurfaceOperationType.NEW, "entities" : qUnion([Q0]), "axis" : qUnion([Q1]), "revolveType" : RevolveType.FULL});
        }
        {
            var Q0;
            Q0=qCreatedBy(makeId("Front.planeOp"),FACE);
            cPlane(context, id + "F16", {"entities" : qUnion([Q0]), "cplaneType" : CPlaneType.OFFSET, "offset" : 16 * mm, "width" : 150 * mm, "height" : 150 * mm});
        }
        {
            var Q0;
            Q0=qCreatedBy(makeId("Front.planeOp"),FACE);
            var sketch = newSketch(context, id + "F17", { "sketchPlane" : qUnion([Q0])});
            skCircle(sketch, "E89", {"center": v(0, 0) * mm, "radius": 13.1 * mm});
            skArc(sketch, "E90", {"start": v(17.5, 0) * mm, "mid": v(0, 17.5) * mm, "end": v(-17.5, 0) * mm});
            skLineSegment(sketch, "E91", {"start": v(0, 0) * mm, "end": v(17.5, 0) * mm, "construction": true});
            skLineSegment(sketch, "E92", {"start": v(0, 0) * mm, "end": v(-17.5, 0) * mm, "construction": true});
            skLineSegment(sketch, "E93", {"start": v(17.5, 0) * mm, "end": v(17.5, -17.5) * mm});
            skLineSegment(sketch, "E94", {"start": v(17.5, -17.5) * mm, "end": v(-17.5, -17.5) * mm});
            skLineSegment(sketch, "E95", {"start": v(-17.5, 0) * mm, "end": v(-17.5, -17.5) * mm});
            skSolve(sketch);
        }
        {
            var Q0;
            Q0=makeQuery(id+"F17.imprint","IMPRINT",FACE,{"disambiguationData":[TD([[makeQuery(id+"F17.imprint","IMPRINT",EDGE,{"derivedFrom":sQuery(id+"F17.wireOp",EDGE,"E89")}),-1.0]])]});
            extrude(context, id + "F18", {"entities" : qUnion([Q0]), "operationType" : NewBodyOperationType.ADD, "depth" : 64 * mm, "offsetDistance" : 25 * mm, "hasSecondDirection" : true, "secondDirectionOppositeDirection" : false, "secondDirectionDepth" : 55 * mm});
        }
        {
            var Q0;
            Q0=makeQuery(id+"F13.opRevolve","SWEPT_BODY",BODY,{"disambiguationData":[OSD([sQuery(id+"F12.wireOp",EDGE,"E75"),sQuery(id+"F12.wireOp",EDGE,"E76"),sQuery(id+"F12.wireOp",EDGE,"E77"),sQuery(id+"F12.wireOp",EDGE,"E78"),sQuery(id+"F12.wireOp",EDGE,"E79"),sQuery(id+"F12.wireOp",EDGE,"E80"),sQuery(id+"F12.wireOp",EDGE,"E81"),sQuery(id+"F12.wireOp",EDGE,"E82")])]});
            var Q1;
            Q1=makeQuery(id+"F14.opRevolve","SWEPT_BODY",BODY,{"disambiguationData":[OSD([sQuery(id+"F12.wireOp",EDGE,"E84.bottom"),sQuery(id+"F12.wireOp",EDGE,"E84.top"),sQuery(id+"F12.wireOp",EDGE,"E84.left"),sQuery(id+"F12.wireOp",EDGE,"E84.right")])]});
            var Q2;
            Q2=makeQuery(id+"F15.opRevolve","SWEPT_BODY",BODY,{"disambiguationData":[OSD([sQuery(id+"F12.wireOp",EDGE,"E85.bottom"),sQuery(id+"F12.wireOp",EDGE,"E85.left"),sQuery(id+"F12.wireOp",EDGE,"E85.right"),sQuery(id+"F12.wireOp",EDGE,"E87.bottom"),sQuery(id+"F12.wireOp",EDGE,"E87.right"),sQuery(id+"F12.wireOp",EDGE,"E88")])]});
            var Q3;
            Q3=qCreatedBy(id+"F16.planeOp",FACE);
            mirror(context, id + "F19", {"entities" : qUnion([Q0, Q1, Q2]), "mirrorPlane" : qUnion([Q3])});
        }
        {
            var Q0;
            Q0=qCreatedBy(makeId("Top.planeOp"),FACE);
            var sketch = newSketch(context, id + "F20", { "sketchPlane" : qUnion([Q0])});
            skLineSegment(sketch, "E96.bottom", {"start": v(-30, 40) * mm, "end": v(30, 40) * mm});
            skLineSegment(sketch, "E96.top", {"start": v(-30, -70) * mm, "end": v(30, -70) * mm});
            skLineSegment(sketch, "E96.left", {"start": v(-30, 40) * mm, "end": v(-30, -70) * mm});
            skLineSegment(sketch, "E96.right", {"start": v(30, 40) * mm, "end": v(30, -70) * mm});
            skLineSegment(sketch, "E97", {"start": v(0, 40) * mm, "end": v(0, -70) * mm, "construction": true});
            skSolve(sketch);
        }
        {
            var Q0;
            Q0 = qSketchRegion(id + "F20", true);
            extrude(context, id + "F21", {"entities" : qUnion([Q0]), "oppositeDirection" : true, "depth" : 22.5 * mm, "offsetDistance" : 25 * mm, "hasSecondDirection" : true, "secondDirectionOppositeDirection" : true, "secondDirectionDepth" : 17.5 * mm});
        }
        {
            var Q0;
            Q0=makeQuery(id+"F21.opExtrude","CAP_FACE",FACE,{"disambiguationData":[OSD([sQuery(id+"F20.wireOp",EDGE,"E96.bottom"),sQuery(id+"F20.wireOp",EDGE,"E96.top"),sQuery(id+"F20.wireOp",EDGE,"E96.left"),sQuery(id+"F20.wireOp",EDGE,"E96.right")])],"isStart":true});
            var sketch = newSketch(context, id + "F22", { "sketchPlane" : qUnion([Q0])});
            skLineSegment(sketch, "E98", {"start": v(-30, 0) * mm, "end": v(30, 0) * mm, "construction": true});
            skLineSegment(sketch, "E99", {"start": v(-30, -25) * mm, "end": v(30, -25) * mm, "construction": true});
            skLineSegment(sketch, "E100.bottom", {"start": v(15.31, 12.5) * mm, "end": v(20.31, 12.5) * mm});
            skLineSegment(sketch, "E100.top", {"start": v(15.31, -37.5) * mm, "end": v(20.31, -37.5) * mm});
            skLineSegment(sketch, "E100.left", {"start": v(15.31, 12.5) * mm, "end": v(15.31, -37.5) * mm});
            skLineSegment(sketch, "E100.right", {"start": v(20.31, 12.5) * mm, "end": v(20.31, -37.5) * mm});
            skLineSegment(sketch, "E101", {"start": v(12.31, 0) * mm, "end": v(12.31, -25) * mm, "construction": true});
            skLineSegment(sketch, "E102", {"start": v(-30, -37.5) * mm, "end": v(30, -37.5) * mm, "construction": true});
            skLineSegment(sketch, "E103", {"start": v(-30, 12.5) * mm, "end": v(30, 12.5) * mm, "construction": true});
            skLineSegment(sketch, "E104", {"start": v(-30, 12.5) * mm, "end": v(-30, 0) * mm, "construction": true});
            skLineSegment(sketch, "E105", {"start": v(-30, -25) * mm, "end": v(-30, -37.5) * mm, "construction": true});
            skLineSegment(sketch, "E106", {"start": v(0, 12.5) * mm, "end": v(0, -37.5) * mm, "construction": true});
            skLineSegment(sketch, "E107.MirrorCS", {"start": v(-15.31, 12.5) * mm, "end": v(-20.31, 12.5) * mm});
            skLineSegment(sketch, "E108.MirrorCS", {"start": v(-15.31, -37.5) * mm, "end": v(-20.31, -37.5) * mm});
            skLineSegment(sketch, "E109.MirrorCS", {"start": v(-20.31, 12.5) * mm, "end": v(-20.31, -37.5) * mm});
            skLineSegment(sketch, "E110.MirrorCS", {"start": v(-15.31, 12.5) * mm, "end": v(-15.31, -37.5) * mm});
            skSolve(sketch);
        }
        {
            var Q0;
            Q0=makeQuery(id+"F22.imprint","IMPRINT",FACE,{"disambiguationData":[TD([[makeQuery(id+"F22.imprint","IMPRINT",EDGE,{"derivedFrom":sQuery(id+"F22.wireOp",EDGE,"E100.bottom")}),-1.0]])]});
            var Q1;
            {var subQ5=sQuery(id+"F22.wireOp",EDGE,"E107.MirrorCS");Q1=makeQuery(id+"F22.imprint","IMPRINT",FACE,{"disambiguationData":[TD([[makeQuery(id+"F22.imprint","IMPRINT",EDGE,{"derivedFrom":subQ5}),1.0]])]});}
            extrude(context, id + "F23", {"entities" : qUnion([Q0, Q1]), "depth" : 27.5 * mm, "offsetDistance" : 25 * mm, "hasSecondDirection" : true, "secondDirectionOppositeDirection" : false, "secondDirectionDepth" : 7.5 * mm});
        }
        {
            var Q0;
            Q0=makeQuery(id+"F22.imprint","IMPRINT",FACE,{"disambiguationData":[TD([[makeQuery(id+"F22.imprint","IMPRINT",EDGE,{"derivedFrom":sQuery(id+"F22.wireOp",EDGE,"E100.bottom")}),1.0]])]});
            var sketch = newSketch(context, id + "F24", { "sketchPlane" : qUnion([Q0])});
            skLineSegment(sketch, "E111.bottom", {"start": v(-22.31, -29) * mm, "end": v(22.31, -29) * mm});
            skLineSegment(sketch, "E111.top", {"start": v(-22.31, -35) * mm, "end": v(22.31, -35) * mm});
            skLineSegment(sketch, "E111.left", {"start": v(-22.31, -29) * mm, "end": v(-22.31, -35) * mm});
            skLineSegment(sketch, "E111.right", {"start": v(22.31, -29) * mm, "end": v(22.31, -35) * mm});
            skSolve(sketch);
        }
        {
            var Q0;
            {var subQ0=sQuery(id+"F24.wireOp",EDGE,"E111.left");Q0=makeQuery(id+"F24.imprint","IMPRINT",FACE,{"disambiguationData":[TD([[makeQuery(id+"F24.imprint","IMPRINT",EDGE,{"derivedFrom":subQ0}),1.0]])]});}
            var Q1;
            {var subQ0=sQuery(id+"F24.wireOp",EDGE,"E111.bottom");var subQ1=makeQuery(id+"F22.imprint","IMPRINT",EDGE,{"derivedFrom":sQuery(id+"F22.wireOp",EDGE,"E109.MirrorCS")});var subQ2=makeQuery(id+"F24.imprint","INTERSECT",VERTEX,{"derivedFrom":[subQ1,subQ0]});Q1=makeQuery(id+"F24.imprint","IMPRINT",FACE,{"disambiguationData":[TD([[makeQuery(id+"F24.imprint","IMPRINT",EDGE,{"disambiguationData":[TD([[subQ2,-1.0]])],"derivedFrom":subQ0}),-1.0]])]});}
            var Q2;
            {var subQ0=sQuery(id+"F24.wireOp",EDGE,"E111.bottom");var subQ1=makeQuery(id+"F22.imprint","IMPRINT",EDGE,{"derivedFrom":sQuery(id+"F22.wireOp",EDGE,"E110.MirrorCS")});var subQ2=makeQuery(id+"F24.imprint","INTERSECT",VERTEX,{"derivedFrom":[subQ1,subQ0]});Q2=makeQuery(id+"F24.imprint","IMPRINT",FACE,{"disambiguationData":[TD([[makeQuery(id+"F24.imprint","IMPRINT",EDGE,{"disambiguationData":[TD([[subQ2,-1.0]])],"derivedFrom":subQ0}),-1.0]])]});}
            var Q3;
            {var subQ0=sQuery(id+"F24.wireOp",EDGE,"E111.bottom");var subQ1=makeQuery(id+"F22.imprint","IMPRINT",EDGE,{"derivedFrom":sQuery(id+"F22.wireOp",EDGE,"E100.left")});var subQ2=makeQuery(id+"F24.imprint","INTERSECT",VERTEX,{"derivedFrom":[subQ1,subQ0]});Q3=makeQuery(id+"F24.imprint","IMPRINT",FACE,{"disambiguationData":[TD([[makeQuery(id+"F24.imprint","IMPRINT",EDGE,{"disambiguationData":[TD([[subQ2,-1.0]])],"derivedFrom":subQ0}),-1.0]])]});}
            var Q4;
            {var subQ0=sQuery(id+"F24.wireOp",EDGE,"E111.right");Q4=makeQuery(id+"F24.imprint","IMPRINT",FACE,{"disambiguationData":[TD([[makeQuery(id+"F24.imprint","IMPRINT",EDGE,{"derivedFrom":subQ0}),-1.0]])]});}
            extrude(context, id + "F25", {"entities" : qUnion([Q0, Q1, Q2, Q3, Q4]), "depth" : 35 * mm, "offsetDistance" : 25 * mm});
        }
        {
            var Q0;
            Q0=makeQuery(id+"F25.opExtrude","CAP_FACE",FACE,{"disambiguationData":[OSD([sQuery(id+"F24.wireOp",EDGE,"E111.bottom"),sQuery(id+"F24.wireOp",EDGE,"E111.top"),sQuery(id+"F24.wireOp",EDGE,"E111.left"),sQuery(id+"F24.wireOp",EDGE,"E111.right")])],"isStart":false});
            var sketch = newSketch(context, id + "F26", { "sketchPlane" : qUnion([Q0])});
            skLineSegment(sketch, "E112", {"start": v(-17.81, -37.5) * mm, "end": v(-17.81, -29) * mm, "construction": true});
            skLineSegment(sketch, "E113", {"start": v(-22.31, -32) * mm, "end": v(22.31, -32) * mm, "construction": true});
            skCircle(sketch, "E114.cCircle", {"center": v(-17.81, -32) * mm, "radius": 0.88 * mm, "construction": true});
            skLineSegment(sketch, "E114.0", {"start": v(-19.06, -32) * mm, "end": v(-17.81, -30.75) * mm});
            skLineSegment(sketch, "E114.1", {"start": v(-17.81, -30.75) * mm, "end": v(-16.56, -32) * mm});
            skLineSegment(sketch, "E114.2", {"start": v(-16.56, -32) * mm, "end": v(-17.81, -33.25) * mm});
            skLineSegment(sketch, "E114.3", {"start": v(-17.81, -33.25) * mm, "end": v(-19.06, -32) * mm});
            skPoint(sketch, "E114.0.midPoint", {"position": v(-18.44, -31.37) * mm});
            skSolve(sketch);
        }
        {
            var Q0;
            Q0=makeQuery(id+"F26.imprint","IMPRINT",FACE,{"disambiguationData":[TD([[makeQuery(id+"F26.imprint","IMPRINT",EDGE,{"derivedFrom":sQuery(id+"F26.wireOp",EDGE,"E114.0")}),-1.0]])]});
            extrude(context, id + "F27", {"entities" : qUnion([Q0]), "oppositeDirection" : true, "depth" : 10 * mm, "offsetDistance" : 25 * mm, "hasSecondDirection" : true, "secondDirectionOppositeDirection" : false, "secondDirectionDepth" : 5 * mm});
        }
        {
            var Q0;
            Q0=makeQuery(id+"F27.opExtrude","SWEPT_BODY",BODY,{"disambiguationData":[OSD([sQuery(id+"F26.wireOp",EDGE,"E114.0"),sQuery(id+"F26.wireOp",EDGE,"E114.1"),sQuery(id+"F26.wireOp",EDGE,"E114.2"),sQuery(id+"F26.wireOp",EDGE,"E114.3")])]});
            var Q1;
            Q1=qCreatedBy(makeId("Right.planeOp"),FACE);
            mirror(context, id + "F28", {"entities" : qUnion([Q0]), "mirrorPlane" : qUnion([Q1])});
        }
        {
            var Q0;
            Q0=makeQuery(id+"F27.opExtrude","SWEPT_BODY",BODY,{"disambiguationData":[OSD([sQuery(id+"F26.wireOp",EDGE,"E114.0"),sQuery(id+"F26.wireOp",EDGE,"E114.1"),sQuery(id+"F26.wireOp",EDGE,"E114.2"),sQuery(id+"F26.wireOp",EDGE,"E114.3")])]});
            var Q1;
            Q1=makeQuery(id+"F28.opPattern","COPY",BODY,{"derivedFrom":makeQuery(id+"F27.opExtrude","SWEPT_BODY",BODY,{"disambiguationData":[OSD([sQuery(id+"F26.wireOp",EDGE,"E114.0"),sQuery(id+"F26.wireOp",EDGE,"E114.1"),sQuery(id+"F26.wireOp",EDGE,"E114.2"),sQuery(id+"F26.wireOp",EDGE,"E114.3")])]}),"instanceName":"1"});
            var Q2;
            Q2=makeQuery(id+"F25.opExtrude","SWEPT_BODY",BODY,{"disambiguationData":[OSD([sQuery(id+"F24.wireOp",EDGE,"E111.bottom"),sQuery(id+"F24.wireOp",EDGE,"E111.top"),sQuery(id+"F24.wireOp",EDGE,"E111.left"),sQuery(id+"F24.wireOp",EDGE,"E111.right")])]});
            booleanBodies(context, id + "F29", {"operationType" : BooleanOperationType.SUBTRACTION, "tools" : qUnion([Q0, Q1]), "targets" : qUnion([Q2])});
        }
        {
            var Q0;
            Q0=makeQuery(id+"F25.opExtrude","SWEPT_FACE",FACE,{"disambiguationData":[OSD([sQuery(id+"F24.wireOp",EDGE,"E111.top")])]});
            var sketch = newSketch(context, id + "F30", { "sketchPlane" : qUnion([Q0])});
            skCircle(sketch, "E115", {"center": v(0, 0) * mm, "radius": 13.5 * mm});
            skLineSegment(sketch, "E116", {"start": v(-20.31, 10) * mm, "end": v(-20.31, -10) * mm, "construction": true});
            skLineSegment(sketch, "E117", {"start": v(-15.31, 10) * mm, "end": v(-15.31, -10) * mm, "construction": true});
            skLineSegment(sketch, "E118", {"start": v(-20.31, 10) * mm, "end": v(-15.31, 10) * mm, "construction": true});
            skLineSegment(sketch, "E119", {"start": v(-20.31, -10) * mm, "end": v(-15.31, -10) * mm, "construction": true});
            skLineSegment(sketch, "E120.0", {"start": v(-20.81, 10.5) * mm, "end": v(-14.81, 10.5) * mm});
            skLineSegment(sketch, "E120.1", {"start": v(-20.81, 10.5) * mm, "end": v(-20.81, -10.5) * mm});
            skLineSegment(sketch, "E120.2", {"start": v(-20.81, -10.5) * mm, "end": v(-14.81, -10.5) * mm});
            skLineSegment(sketch, "E120.3", {"start": v(-14.81, 10.5) * mm, "end": v(-14.81, -10.5) * mm});
            skLineSegment(sketch, "E121", {"start": v(0, 17.5) * mm, "end": v(0, -17.5) * mm, "construction": true});
            skLineSegment(sketch, "E122.MirrorCS", {"start": v(20.81, 10.5) * mm, "end": v(14.81, 10.5) * mm});
            skLineSegment(sketch, "E123.MirrorCS", {"start": v(14.81, 10.5) * mm, "end": v(14.81, -10.5) * mm});
            skLineSegment(sketch, "E124.MirrorCS", {"start": v(20.81, 10.5) * mm, "end": v(20.81, -10.5) * mm});
            skLineSegment(sketch, "E125.MirrorCS", {"start": v(20.81, -10.5) * mm, "end": v(14.81, -10.5) * mm});
            skSolve(sketch);
        }
        {
            var Q0;
            Q0=makeQuery(id+"F30.imprint","IMPRINT",FACE,{"disambiguationData":[TD([[makeQuery(id+"F30.imprint","IMPRINT",EDGE,{"derivedFrom":sQuery(id+"F30.wireOp",EDGE,"E115")}),1.0]])]});
            var Q1;
            Q1=makeQuery(id+"F30.imprint","IMPRINT",FACE,{"disambiguationData":[TD([[makeQuery(id+"F30.imprint","IMPRINT",EDGE,{"derivedFrom":sQuery(id+"F30.wireOp",EDGE,"E120.0")}),-1.0]])]});
            var Q2;
            Q2=makeQuery(id+"F30.imprint","IMPRINT",FACE,{"disambiguationData":[TD([[makeQuery(id+"F30.imprint","IMPRINT",EDGE,{"derivedFrom":sQuery(id+"F30.wireOp",EDGE,"E122.MirrorCS")}),1.0]])]});
            extrude(context, id + "F31", {"entities" : qUnion([Q0, Q1, Q2]), "operationType" : NewBodyOperationType.REMOVE, "oppositeDirection" : true, "depth" : 10 * mm, "offsetDistance" : 25 * mm});
        }
        {
            var Q0;
            Q0=makeQuery(id+"F23.opExtrude","SWEPT_FACE",FACE,{"disambiguationData":[OSD([sQuery(id+"F22.wireOp",EDGE,"E100.top")])]});
            var Q1;
            Q1=makeQuery(id+"F23.opExtrude","SWEPT_FACE",FACE,{"disambiguationData":[OSD([sQuery(id+"F22.wireOp",EDGE,"E107.MirrorCS")])]});
            cPlane(context, id + "F32", {"entities" : qUnion([Q0, Q1]), "cplaneType" : CPlaneType.MID_PLANE, "offset" : 25 * mm, "flipAlignment" : true, "width" : 150 * mm, "height" : 150 * mm});
        }
        {
            var Q0;
            Q0=makeQuery(id+"F25.opExtrude","CAP_EDGE",EDGE,{"disambiguationData":[OSD([sQuery(id+"F24.wireOp",EDGE,"E111.right")])],"isStart":false});
            var Q1;
            Q1=makeQuery(id+"F25.opExtrude","CAP_EDGE",EDGE,{"disambiguationData":[OSD([sQuery(id+"F24.wireOp",EDGE,"E111.left")])],"isStart":false});
            fillet(context, id + "F33", {"entities" : qUnion([Q0, Q1]), "radius" : 2 * mm, "tangentPropagation" : true, "allowEdgeOverflow" : false});
        }
        {
            var Q0;
            Q0=makeQuery(id+"F25.opExtrude","SWEPT_BODY",BODY,{"disambiguationData":[OSD([sQuery(id+"F24.wireOp",EDGE,"E111.bottom"),sQuery(id+"F24.wireOp",EDGE,"E111.top"),sQuery(id+"F24.wireOp",EDGE,"E111.left"),sQuery(id+"F24.wireOp",EDGE,"E111.right")])]});
            var Q1;
            Q1=qCreatedBy(id+"F32.planeOp",FACE);
            mirror(context, id + "F34", {"operationType" : NewBodyOperationType.ADD, "entities" : qUnion([Q0]), "mirrorPlane" : qUnion([Q1])});
        }
        {
            var Q0;
            Q0=makeQuery(id+"F21.opExtrude","CAP_FACE",FACE,{"disambiguationData":[OSD([sQuery(id+"F20.wireOp",EDGE,"E96.bottom"),sQuery(id+"F20.wireOp",EDGE,"E96.top"),sQuery(id+"F20.wireOp",EDGE,"E96.left"),sQuery(id+"F20.wireOp",EDGE,"E96.right")])],"isStart":false});
            var sketch = newSketch(context, id + "F35", { "sketchPlane" : qUnion([Q0])});
            skLineSegment(sketch, "E126", {"start": v(-30, 32) * mm, "end": v(74.63, 32) * mm, "construction": true});
            skLineSegment(sketch, "E127", {"start": v(-30, -7) * mm, "end": v(74.63, -7) * mm, "construction": true});
            skLineSegment(sketch, "E128", {"start": v(14.5, -40) * mm, "end": v(14.5, 70) * mm, "construction": true});
            skLineSegment(sketch, "E129", {"start": v(-14.5, -40) * mm, "end": v(-14.5, 70) * mm, "construction": true});
            skLineSegment(sketch, "E130", {"start": v(-30, -27.5) * mm, "end": v(17.5, -27.5) * mm, "construction": true});
            skLineSegment(sketch, "E131", {"start": v(17.5, 59.5) * mm, "end": v(-30, 59.5) * mm, "construction": true});
            skCircle(sketch, "E132", {"center": v(-14.5, 59.5) * mm, "radius": 1.5 * mm});
            skCircle(sketch, "E133", {"center": v(14.5, 59.5) * mm, "radius": 1.5 * mm});
            skCircle(sketch, "E134", {"center": v(14.5, -27.5) * mm, "radius": 1.5 * mm});
            skCircle(sketch, "E135", {"center": v(-14.5, -27.5) * mm, "radius": 1.5 * mm});
            skCircle(sketch, "E136", {"center": v(14.5, 59.5) * mm, "radius": 0.5 * mm});
            skCircle(sketch, "E137", {"center": v(-14.5, 59.5) * mm, "radius": 0.5 * mm});
            skCircle(sketch, "E138", {"center": v(14.5, -27.5) * mm, "radius": 0.5 * mm});
            skCircle(sketch, "E139", {"center": v(-14.5, -27.5) * mm, "radius": 0.5 * mm});
            skCircle(sketch, "E140", {"center": v(-14.5, 32) * mm, "radius": 1.5 * mm});
            skCircle(sketch, "E141", {"center": v(14.5, 32) * mm, "radius": 0.5 * mm});
            skCircle(sketch, "E142", {"center": v(14.5, 32) * mm, "radius": 1.5 * mm});
            skCircle(sketch, "E143", {"center": v(-14.5, 32) * mm, "radius": 0.5 * mm});
            skCircle(sketch, "E144", {"center": v(14.5, -7) * mm, "radius": 0.5 * mm});
            skCircle(sketch, "E145", {"center": v(14.5, -7) * mm, "radius": 1.5 * mm});
            skCircle(sketch, "E146", {"center": v(-14.5, -7) * mm, "radius": 0.5 * mm});
            skCircle(sketch, "E147", {"center": v(-14.5, -7) * mm, "radius": 1.5 * mm});
            skSolve(sketch);
        }
        {
            var Q0;
            Q0=makeQuery(id+"F35.imprint","IMPRINT",FACE,{"disambiguationData":[TD([[makeQuery(id+"F35.imprint","IMPRINT",EDGE,{"derivedFrom":sQuery(id+"F35.wireOp",EDGE,"E132")}),1.0]])]});
            var Q1;
            Q1=makeQuery(id+"F35.imprint","IMPRINT",FACE,{"disambiguationData":[TD([[makeQuery(id+"F35.imprint","IMPRINT",EDGE,{"derivedFrom":sQuery(id+"F35.wireOp",EDGE,"E137")}),1.0]])]});
            var Q2;
            Q2=makeQuery(id+"F35.imprint","IMPRINT",FACE,{"disambiguationData":[TD([[makeQuery(id+"F35.imprint","IMPRINT",EDGE,{"derivedFrom":sQuery(id+"F35.wireOp",EDGE,"E136")}),1.0]])]});
            var Q3;
            Q3=makeQuery(id+"F35.imprint","IMPRINT",FACE,{"disambiguationData":[TD([[makeQuery(id+"F35.imprint","IMPRINT",EDGE,{"derivedFrom":sQuery(id+"F35.wireOp",EDGE,"E133")}),1.0]])]});
            var Q4;
            Q4=makeQuery(id+"F35.imprint","IMPRINT",FACE,{"disambiguationData":[TD([[makeQuery(id+"F35.imprint","IMPRINT",EDGE,{"derivedFrom":sQuery(id+"F35.wireOp",EDGE,"PFyNPDqs-Ep8R-HGao-31Ur-gI6ej4vQ4cxJ")}),1.0]])]});
            var Q5;
            Q5=makeQuery(id+"F35.imprint","IMPRINT",FACE,{"disambiguationData":[TD([[makeQuery(id+"F35.imprint","IMPRINT",EDGE,{"derivedFrom":sQuery(id+"F35.wireOp",EDGE,"Kp0F8KkM-gTSG-8IrS-7Ek4-cIwRPN5PFipR")}),1.0]])]});
            var Q6;
            Q6=makeQuery(id+"F35.imprint","IMPRINT",FACE,{"disambiguationData":[TD([[makeQuery(id+"F35.imprint","IMPRINT",EDGE,{"derivedFrom":sQuery(id+"F35.wireOp",EDGE,"OavnT1iM-PWWg-e2RI-Cgqf-CRE9zpLMibSG")}),1.0]])]});
            var Q7;
            Q7=makeQuery(id+"F35.imprint","IMPRINT",FACE,{"disambiguationData":[TD([[makeQuery(id+"F35.imprint","IMPRINT",EDGE,{"derivedFrom":sQuery(id+"F35.wireOp",EDGE,"6iWuaM59-P9UH-9INN-MEdt-I3GYd4iT0KjY")}),1.0]])]});
            var Q8;
            Q8=makeQuery(id+"F35.imprint","IMPRINT",FACE,{"disambiguationData":[TD([[makeQuery(id+"F35.imprint","IMPRINT",EDGE,{"derivedFrom":sQuery(id+"F35.wireOp",EDGE,"GS8uUdpl-7a4f-zSQ8-zMdr-q3VKJ9zmA7Z2")}),1.0]])]});
            var Q9;
            Q9=makeQuery(id+"F35.imprint","IMPRINT",FACE,{"disambiguationData":[TD([[makeQuery(id+"F35.imprint","IMPRINT",EDGE,{"derivedFrom":sQuery(id+"F35.wireOp",EDGE,"F0IPPkhX-6PCt-gYH3-62Ki-m6P0bRLTlL1H")}),1.0]])]});
            var Q10;
            Q10=makeQuery(id+"F35.imprint","IMPRINT",FACE,{"disambiguationData":[TD([[makeQuery(id+"F35.imprint","IMPRINT",EDGE,{"derivedFrom":sQuery(id+"F35.wireOp",EDGE,"SXbGrNF4-FH9E-IirH-lWky-iFOXS6nttWAW")}),1.0]])]});
            var Q11;
            Q11=makeQuery(id+"F35.imprint","IMPRINT",FACE,{"disambiguationData":[TD([[makeQuery(id+"F35.imprint","IMPRINT",EDGE,{"derivedFrom":sQuery(id+"F35.wireOp",EDGE,"XRTzMnL4-Fk8b-kX3F-CXxC-4Bn30n7xDRgZ")}),1.0]])]});
            var Q12;
            Q12=makeQuery(id+"F35.imprint","IMPRINT",FACE,{"disambiguationData":[TD([[makeQuery(id+"F35.imprint","IMPRINT",EDGE,{"derivedFrom":sQuery(id+"F35.wireOp",EDGE,"E138")}),1.0]])]});
            var Q13;
            Q13=makeQuery(id+"F35.imprint","IMPRINT",FACE,{"disambiguationData":[TD([[makeQuery(id+"F35.imprint","IMPRINT",EDGE,{"derivedFrom":sQuery(id+"F35.wireOp",EDGE,"E134")}),1.0]])]});
            var Q14;
            Q14=makeQuery(id+"F35.imprint","IMPRINT",FACE,{"disambiguationData":[TD([[makeQuery(id+"F35.imprint","IMPRINT",EDGE,{"derivedFrom":sQuery(id+"F35.wireOp",EDGE,"E139")}),1.0]])]});
            var Q15;
            Q15=makeQuery(id+"F35.imprint","IMPRINT",FACE,{"disambiguationData":[TD([[makeQuery(id+"F35.imprint","IMPRINT",EDGE,{"derivedFrom":sQuery(id+"F35.wireOp",EDGE,"E135")}),1.0]])]});
            var Q16;
            Q16=makeQuery(id+"F35.imprint","IMPRINT",FACE,{"disambiguationData":[TD([[makeQuery(id+"F35.imprint","IMPRINT",EDGE,{"derivedFrom":sQuery(id+"F35.wireOp",EDGE,"E141")}),-1.0]])]});
            var Q17;
            Q17=makeQuery(id+"F35.imprint","IMPRINT",FACE,{"disambiguationData":[TD([[makeQuery(id+"F35.imprint","IMPRINT",EDGE,{"derivedFrom":sQuery(id+"F35.wireOp",EDGE,"E141")}),1.0]])]});
            var Q18;
            Q18=makeQuery(id+"F35.imprint","IMPRINT",FACE,{"disambiguationData":[TD([[makeQuery(id+"F35.imprint","IMPRINT",EDGE,{"derivedFrom":sQuery(id+"F35.wireOp",EDGE,"E140")}),1.0]])]});
            var Q19;
            Q19=makeQuery(id+"F35.imprint","IMPRINT",FACE,{"disambiguationData":[TD([[makeQuery(id+"F35.imprint","IMPRINT",EDGE,{"derivedFrom":sQuery(id+"F35.wireOp",EDGE,"E143")}),1.0]])]});
            var Q20;
            Q20=makeQuery(id+"F35.imprint","IMPRINT",FACE,{"disambiguationData":[TD([[makeQuery(id+"F35.imprint","IMPRINT",EDGE,{"derivedFrom":sQuery(id+"F35.wireOp",EDGE,"E144")}),-1.0]])]});
            var Q21;
            Q21=makeQuery(id+"F35.imprint","IMPRINT",FACE,{"disambiguationData":[TD([[makeQuery(id+"F35.imprint","IMPRINT",EDGE,{"derivedFrom":sQuery(id+"F35.wireOp",EDGE,"E144")}),1.0]])]});
            var Q22;
            Q22=makeQuery(id+"F35.imprint","IMPRINT",FACE,{"disambiguationData":[TD([[makeQuery(id+"F35.imprint","IMPRINT",EDGE,{"derivedFrom":sQuery(id+"F35.wireOp",EDGE,"E146")}),1.0]])]});
            var Q23;
            Q23=makeQuery(id+"F35.imprint","IMPRINT",FACE,{"disambiguationData":[TD([[makeQuery(id+"F35.imprint","IMPRINT",EDGE,{"derivedFrom":sQuery(id+"F35.wireOp",EDGE,"E146")}),-1.0]])]});
            extrude(context, id + "F36", {"entities" : qUnion([Q0, Q1, Q2, Q3, Q4, Q5, Q6, Q7, Q8, Q9, Q10, Q11, Q12, Q13, Q14, Q15, Q16, Q17, Q18, Q19, Q20, Q21, Q22, Q23]), "operationType" : NewBodyOperationType.REMOVE, "oppositeDirection" : true, "depth" : 5 * mm, "offsetDistance" : 25 * mm});
        }
        {
            var Q0;
            Q0=makeQuery(id+"F35.imprint","IMPRINT",FACE,{"disambiguationData":[TD([[makeQuery(id+"F35.imprint","IMPRINT",EDGE,{"derivedFrom":sQuery(id+"F35.wireOp",EDGE,"E137")}),1.0]])]});
            var Q1;
            Q1=makeQuery(id+"F35.imprint","IMPRINT",FACE,{"disambiguationData":[TD([[makeQuery(id+"F35.imprint","IMPRINT",EDGE,{"derivedFrom":sQuery(id+"F35.wireOp",EDGE,"E136")}),1.0]])]});
            var Q2;
            Q2=makeQuery(id+"F35.imprint","IMPRINT",FACE,{"disambiguationData":[TD([[makeQuery(id+"F35.imprint","IMPRINT",EDGE,{"derivedFrom":sQuery(id+"F35.wireOp",EDGE,"Kp0F8KkM-gTSG-8IrS-7Ek4-cIwRPN5PFipR")}),1.0]])]});
            var Q3;
            Q3=makeQuery(id+"F35.imprint","IMPRINT",FACE,{"disambiguationData":[TD([[makeQuery(id+"F35.imprint","IMPRINT",EDGE,{"derivedFrom":sQuery(id+"F35.wireOp",EDGE,"OavnT1iM-PWWg-e2RI-Cgqf-CRE9zpLMibSG")}),1.0]])]});
            var Q4;
            Q4=makeQuery(id+"F35.imprint","IMPRINT",FACE,{"disambiguationData":[TD([[makeQuery(id+"F35.imprint","IMPRINT",EDGE,{"derivedFrom":sQuery(id+"F35.wireOp",EDGE,"SXbGrNF4-FH9E-IirH-lWky-iFOXS6nttWAW")}),1.0]])]});
            var Q5;
            Q5=makeQuery(id+"F35.imprint","IMPRINT",FACE,{"disambiguationData":[TD([[makeQuery(id+"F35.imprint","IMPRINT",EDGE,{"derivedFrom":sQuery(id+"F35.wireOp",EDGE,"GS8uUdpl-7a4f-zSQ8-zMdr-q3VKJ9zmA7Z2")}),1.0]])]});
            var Q6;
            Q6=makeQuery(id+"F35.imprint","IMPRINT",FACE,{"disambiguationData":[TD([[makeQuery(id+"F35.imprint","IMPRINT",EDGE,{"derivedFrom":sQuery(id+"F35.wireOp",EDGE,"E139")}),1.0]])]});
            var Q7;
            Q7=makeQuery(id+"F35.imprint","IMPRINT",FACE,{"disambiguationData":[TD([[makeQuery(id+"F35.imprint","IMPRINT",EDGE,{"derivedFrom":sQuery(id+"F35.wireOp",EDGE,"E138")}),1.0]])]});
            var Q8;
            Q8=makeQuery(id+"F35.imprint","IMPRINT",FACE,{"disambiguationData":[TD([[makeQuery(id+"F35.imprint","IMPRINT",EDGE,{"derivedFrom":sQuery(id+"F35.wireOp",EDGE,"E141")}),1.0]])]});
            var Q9;
            Q9=makeQuery(id+"F35.imprint","IMPRINT",FACE,{"disambiguationData":[TD([[makeQuery(id+"F35.imprint","IMPRINT",EDGE,{"derivedFrom":sQuery(id+"F35.wireOp",EDGE,"E143")}),1.0]])]});
            var Q10;
            Q10=makeQuery(id+"F35.imprint","IMPRINT",FACE,{"disambiguationData":[TD([[makeQuery(id+"F35.imprint","IMPRINT",EDGE,{"derivedFrom":sQuery(id+"F35.wireOp",EDGE,"E144")}),1.0]])]});
            var Q11;
            Q11=makeQuery(id+"F35.imprint","IMPRINT",FACE,{"disambiguationData":[TD([[makeQuery(id+"F35.imprint","IMPRINT",EDGE,{"derivedFrom":sQuery(id+"F35.wireOp",EDGE,"E146")}),1.0]])]});
            extrude(context, id + "F37", {"entities" : qUnion([Q0, Q1, Q2, Q3, Q4, Q5, Q6, Q7, Q8, Q9, Q10, Q11]), "operationType" : NewBodyOperationType.REMOVE, "oppositeDirection" : true, "depth" : 10 * mm, "offsetDistance" : 25 * mm});
        }
        {
            var Q0;
            Q0=makeQuery(id+"F21.opExtrude","SWEPT_EDGE",EDGE,{"disambiguationData":[OSD([sQuery(id+"F20.wireOp",EDGE,"E96.top"),sQuery(id+"F20.wireOp",EDGE,"E96.left")])]});
            var Q1;
            Q1=makeQuery(id+"F21.opExtrude","SWEPT_EDGE",EDGE,{"disambiguationData":[OSD([sQuery(id+"F20.wireOp",EDGE,"E96.top"),sQuery(id+"F20.wireOp",EDGE,"E96.right")])]});
            var Q2;
            Q2=makeQuery(id+"F21.opExtrude","SWEPT_EDGE",EDGE,{"disambiguationData":[OSD([sQuery(id+"F20.wireOp",EDGE,"E96.bottom"),sQuery(id+"F20.wireOp",EDGE,"E96.right")])]});
            var Q3;
            Q3=makeQuery(id+"F21.opExtrude","SWEPT_EDGE",EDGE,{"disambiguationData":[OSD([sQuery(id+"F20.wireOp",EDGE,"E96.bottom"),sQuery(id+"F20.wireOp",EDGE,"E96.left")])]});
            fillet(context, id + "F38", {"entities" : qUnion([Q0, Q1, Q2, Q3]), "radius" : 5 * mm, "tangentPropagation" : true, "allowEdgeOverflow" : false});
        }
        {
            var Q0;
            Q0=makeQuery(id+"F10.opRevolve","SWEPT_FACE",FACE,{"disambiguationData":[OSD([sQuery(id+"F9.wireOp",EDGE,"E72")])]});
            var sketch = newSketch(context, id + "F39", { "sketchPlane" : qUnion([Q0])});
            skLineSegment(sketch, "E148", {"start": v(7.25, 14.68) * mm, "end": v(7.25, -16) * mm, "construction": true});
            skLineSegment(sketch, "E149", {"start": v(-22.31, 8) * mm, "end": v(30, 8) * mm, "construction": true});
            skLineSegment(sketch, "E150", {"start": v(-22.31, -8) * mm, "end": v(8.75, -8) * mm, "construction": true});
            skArc(sketch, "E151", {"start": v(10.25, 9.47) * mm, "mid": v(8.16, 10.88) * mm, "end": v(7.73, 8.4) * mm});
            skLineSegment(sketch, "E152", {"start": v(13.75, -17.5) * mm, "end": v(30, -17.5) * mm});
            skLineSegment(sketch, "E153", {"start": v(30, -17.5) * mm, "end": v(30, -8.11) * mm});
            skLineSegment(sketch, "E154", {"start": v(25.6, -4.04) * mm, "end": v(24.86, -4.04) * mm});
            skLineSegment(sketch, "E155", {"start": v(25.6, -4.04) * mm, "end": v(9.77, 10.6) * mm, "construction": true});
            skArc(sketch, "E156", {"start": v(8.75, -8) * mm, "mid": v(7.25, -9.5) * mm, "end": v(8.75, -11) * mm});
            skLineSegment(sketch, "E157", {"start": v(7.25, -11) * mm, "end": v(8.75, -11) * mm, "construction": true});
            skLineSegment(sketch, "E158", {"start": v(13.25, -12) * mm, "end": v(7.25, -12) * mm});
            skLineSegment(sketch, "E159", {"start": v(7.25, -12) * mm, "end": v(7.25, -16) * mm});
            skLineSegment(sketch, "E160", {"start": v(8.75, -11) * mm, "end": v(13.25, -11) * mm});
            skLineSegment(sketch, "E161", {"start": v(10.25, 9.47) * mm, "end": v(24.86, -4.04) * mm});
            skLineSegment(sketch, "E162", {"start": v(7.73, 8.4) * mm, "end": v(13.2, 3.35) * mm});
            skLineSegment(sketch, "E163", {"start": v(8.75, -8) * mm, "end": v(8.75, -8) * mm});
            skArc(sketch, "E164.filletArc", {"start": v(8.75, -8) * mm, "mid": v(14.84, -3.84) * mm, "end": v(13.2, 3.35) * mm});
            skLineSegment(sketch, "E165", {"start": v(17.52, 3.43) * mm, "end": v(24.86, -3.36) * mm, "construction": true});
            skLineSegment(sketch, "E166", {"start": v(24.86, -3.36) * mm, "end": v(28.46, 0.53) * mm, "construction": true});
            skLineSegment(sketch, "E167", {"start": v(28.46, 0.53) * mm, "end": v(21.12, 7.32) * mm, "construction": true});
            skLineSegment(sketch, "E168", {"start": v(21.12, 7.32) * mm, "end": v(17.52, 3.43) * mm, "construction": true});
            skLineSegment(sketch, "E169", {"start": v(13.25, -12) * mm, "end": v(13.25, -11) * mm});
            skPoint(sketch, "E170.visualSharp", {"position": v(25.6, -4.04) * mm});
            skLineSegment(sketch, "E171", {"start": v(25.6, -4.04) * mm, "end": v(30, -8.11) * mm});
            skLineSegment(sketch, "E172", {"start": v(28.9, -7.1) * mm, "end": v(24.82, -11.5) * mm, "construction": true});
            skLineSegment(sketch, "E173", {"start": v(26.7, -5.06) * mm, "end": v(22.62, -9.46) * mm, "construction": true});
            skLineSegment(sketch, "E174", {"start": v(22.62, -9.46) * mm, "end": v(24.82, -11.5) * mm, "construction": true});
            skLineSegment(sketch, "E175", {"start": v(12.25, -12) * mm, "end": v(12.25, -17.5) * mm, "construction": true});
            skLineSegment(sketch, "E176", {"start": v(9.25, -12) * mm, "end": v(9.25, -17.5) * mm, "construction": true});
            skLineSegment(sketch, "E177", {"start": v(7.25, -16) * mm, "end": v(13.75, -16) * mm});
            skLineSegment(sketch, "E178", {"start": v(13.75, -16) * mm, "end": v(13.75, -17.5) * mm});
            skLineSegment(sketch, "E179", {"start": v(18, -9.5) * mm, "end": v(18, -17.5) * mm, "construction": true});
            skLineSegment(sketch, "E180", {"start": v(19.5, -9.5) * mm, "end": v(19.5, -17.5) * mm, "construction": true});
            skLineSegment(sketch, "E181", {"start": v(16.5, -9.5) * mm, "end": v(16.5, -17.5) * mm, "construction": true});
            skLineSegment(sketch, "E182", {"start": v(16.5, -9.5) * mm, "end": v(19.5, -9.5) * mm, "construction": true});
            skSolve(sketch);
        }
        {
            var Q0;
            Q0=makeQuery(id+"F39.imprint","IMPRINT",FACE,{"disambiguationData":[TD([[makeQuery(id+"F39.imprint","IMPRINT",EDGE,{"derivedFrom":sQuery(id+"F39.wireOp",EDGE,"E151")}),1.0]])]});
            extrude(context, id + "F40", {"entities" : qUnion([Q0]), "oppositeDirection" : true, "depth" : 7 * mm, "offsetDistance" : 25 * mm, "hasSecondDirection" : true, "secondDirectionOppositeDirection" : true, "secondDirectionDepth" : 2 * mm});
        }
        {
            var Q0;
            Q0=makeQuery(id+"F40.opExtrude","SWEPT_FACE",FACE,{"disambiguationData":[OSD([sQuery(id+"F39.wireOp",EDGE,"E171")])]});
            var sketch = newSketch(context, id + "F41", { "sketchPlane" : qUnion([Q0])});
            skLineSegment(sketch, "E183", {"start": v(24.53, -46) * mm, "end": v(24.53, -41) * mm, "construction": true});
            skLineSegment(sketch, "E184", {"start": v(23.03, -48) * mm, "end": v(26.03, -48) * mm, "construction": true});
            skLineSegment(sketch, "E185", {"start": v(24.53, -48) * mm, "end": v(24.53, -46) * mm, "construction": true});
            skCircle(sketch, "E186.cCircle", {"center": v(24.53, -43.5) * mm, "radius": 0.88 * mm, "construction": true});
            skLineSegment(sketch, "E186.0", {"start": v(23.28, -43.5) * mm, "end": v(24.53, -42.25) * mm});
            skLineSegment(sketch, "E186.1", {"start": v(24.53, -42.25) * mm, "end": v(25.78, -43.5) * mm});
            skLineSegment(sketch, "E186.2", {"start": v(25.78, -43.5) * mm, "end": v(24.53, -44.75) * mm});
            skLineSegment(sketch, "E186.3", {"start": v(24.53, -44.75) * mm, "end": v(23.28, -43.5) * mm});
            skPoint(sketch, "E186.0.midPoint", {"position": v(23.9, -42.88) * mm});
            skLineSegment(sketch, "E187", {"start": v(24.53, -43.5) * mm, "end": v(23.28, -43.5) * mm, "construction": true});
            skSolve(sketch);
        }
        {
            var Q0;
            Q0=makeQuery(id+"F41.imprint","IMPRINT",FACE,{"disambiguationData":[TD([[makeQuery(id+"F41.imprint","IMPRINT",EDGE,{"derivedFrom":sQuery(id+"F41.wireOp",EDGE,"E186.0")}),-1.0]])]});
            extrude(context, id + "F42", {"entities" : qUnion([Q0]), "operationType" : NewBodyOperationType.REMOVE, "oppositeDirection" : true, "depth" : 7 * mm, "offsetDistance" : 25 * mm});
        }
        {
            var Q0;
            Q0=makeQuery(id+"F40.opExtrude","SWEPT_FACE",FACE,{"disambiguationData":[OSD([sQuery(id+"F39.wireOp",EDGE,"E177")])]});
            var sketch = newSketch(context, id + "F43", { "sketchPlane" : qUnion([Q0])});
            skLineSegment(sketch, "E188", {"start": v(10.75, 46) * mm, "end": v(10.75, 41) * mm, "construction": true});
            skLineSegment(sketch, "E189", {"start": v(12.25, 48) * mm, "end": v(9.25, 48) * mm, "construction": true});
            skLineSegment(sketch, "E190", {"start": v(10.75, 48) * mm, "end": v(10.75, 46) * mm, "construction": true});
            skCircle(sketch, "E191.cCircle", {"center": v(10.75, 43.5) * mm, "radius": 0.88 * mm, "construction": true});
            skLineSegment(sketch, "E191.0", {"start": v(12, 43.5) * mm, "end": v(10.75, 42.25) * mm});
            skLineSegment(sketch, "E191.1", {"start": v(10.75, 42.25) * mm, "end": v(9.5, 43.5) * mm});
            skLineSegment(sketch, "E191.2", {"start": v(9.5, 43.5) * mm, "end": v(10.75, 44.75) * mm});
            skLineSegment(sketch, "E191.3", {"start": v(10.75, 44.75) * mm, "end": v(12, 43.5) * mm});
            skPoint(sketch, "E191.0.midPoint", {"position": v(11.38, 42.88) * mm});
            skSolve(sketch);
        }
        {
            var Q0;
            Q0=makeQuery(id+"F43.imprint","IMPRINT",FACE,{"disambiguationData":[TD([[makeQuery(id+"F43.imprint","IMPRINT",EDGE,{"derivedFrom":sQuery(id+"F43.wireOp",EDGE,"E191.0")}),-1.0]])]});
            extrude(context, id + "F44", {"entities" : qUnion([Q0]), "operationType" : NewBodyOperationType.REMOVE, "oppositeDirection" : true, "depth" : 4.5 * mm, "offsetDistance" : 25 * mm});
        }
        {
            var Q0;
            Q0=makeQuery(id+"F21.opExtrude","CAP_FACE",FACE,{"disambiguationData":[OSD([sQuery(id+"F20.wireOp",EDGE,"E96.bottom"),sQuery(id+"F20.wireOp",EDGE,"E96.top"),sQuery(id+"F20.wireOp",EDGE,"E96.left"),sQuery(id+"F20.wireOp",EDGE,"E96.right")])],"isStart":true});
            var sketch = newSketch(context, id + "F45", { "sketchPlane" : qUnion([Q0])});
            skLineSegment(sketch, "E192", {"start": v(18, -48) * mm, "end": v(18, -46) * mm, "construction": true});
            skLineSegment(sketch, "E193", {"start": v(18, -46) * mm, "end": v(18, -41) * mm, "construction": true});
            skCircle(sketch, "E194.cCircle", {"center": v(18, -43.5) * mm, "radius": 0.88 * mm, "construction": true});
            skLineSegment(sketch, "E194.0", {"start": v(19.25, -43.5) * mm, "end": v(18, -44.75) * mm});
            skLineSegment(sketch, "E194.1", {"start": v(18, -44.75) * mm, "end": v(16.75, -43.5) * mm});
            skLineSegment(sketch, "E194.2", {"start": v(16.75, -43.5) * mm, "end": v(18, -42.25) * mm});
            skLineSegment(sketch, "E194.3", {"start": v(18, -42.25) * mm, "end": v(19.25, -43.5) * mm});
            skPoint(sketch, "E194.0.midPoint", {"position": v(18.62, -44.12) * mm});
            skCircle(sketch, "E195", {"center": v(18, -43.5) * mm, "radius": 1.75 * mm});
            skCircle(sketch, "E196", {"center": v(10.75, -43.5) * mm, "radius": 3 * mm});
            skLineSegment(sketch, "E197.bottom", {"start": v(-30, -46.25) * mm, "end": v(30, -46.25) * mm});
            skLineSegment(sketch, "E197.top", {"start": v(-30, -48.25) * mm, "end": v(30, -48.25) * mm});
            skLineSegment(sketch, "E197.left", {"start": v(-30, -46.25) * mm, "end": v(-30, -48.25) * mm});
            skLineSegment(sketch, "E197.right", {"start": v(30, -46.25) * mm, "end": v(30, -48.25) * mm});
            skLineSegment(sketch, "E198.bottom", {"start": v(-30, -38.75) * mm, "end": v(30, -38.75) * mm});
            skLineSegment(sketch, "E198.top", {"start": v(-30, -40.75) * mm, "end": v(30, -40.75) * mm});
            skLineSegment(sketch, "E198.left", {"start": v(-30, -38.75) * mm, "end": v(-30, -40.75) * mm});
            skLineSegment(sketch, "E198.right", {"start": v(30, -38.75) * mm, "end": v(30, -40.75) * mm});
            skSolve(sketch);
        }
        {
            var Q0;
            Q0=makeQuery(id+"F45.imprint","IMPRINT",FACE,{"disambiguationData":[TD([[makeQuery(id+"F45.imprint","IMPRINT",EDGE,{"derivedFrom":sQuery(id+"F45.wireOp",EDGE,"E196")}),1.0]])]});
            var Q1;
            {var subQ0=sQuery(id+"F45.wireOp",EDGE,"E197.bottom");var subQ1=sQuery(id+"F45.wireOp",EDGE,"E196");var subQ2=makeQuery(id+"F45.imprint","INTERSECT",VERTEX,{"disambiguationData":[OD(0.0)],"derivedFrom":[subQ1,subQ0]});Q1=makeQuery(id+"F45.imprint","IMPRINT",FACE,{"disambiguationData":[TD([[makeQuery(id+"F45.imprint","IMPRINT",EDGE,{"disambiguationData":[TD([[subQ2,-1.0]])],"derivedFrom":subQ1}),1.0]])]});}
            var Q2;
            {var subQ0=sQuery(id+"F45.wireOp",EDGE,"E198.top");var subQ1=sQuery(id+"F45.wireOp",EDGE,"E196");var subQ2=makeQuery(id+"F45.imprint","INTERSECT",VERTEX,{"disambiguationData":[OD(0.0)],"derivedFrom":[subQ1,subQ0]});Q2=makeQuery(id+"F45.imprint","IMPRINT",FACE,{"disambiguationData":[TD([[makeQuery(id+"F45.imprint","IMPRINT",EDGE,{"disambiguationData":[TD([[subQ2,1.0]])],"derivedFrom":subQ1}),1.0]])]});}
            extrude(context, id + "F46", {"entities" : qUnion([Q0, Q1, Q2]), "oppositeDirection" : true, "depth" : 10 * mm, "offsetDistance" : 25 * mm});
        }
        {
            var Q0;
            Q0=makeQuery(id+"F45.imprint","IMPRINT",FACE,{"disambiguationData":[TD([[makeQuery(id+"F45.imprint","IMPRINT",EDGE,{"derivedFrom":sQuery(id+"F45.wireOp",EDGE,"E194.0")}),1.0]])]});
            var Q1;
            Q1=makeQuery(id+"F45.imprint","IMPRINT",FACE,{"disambiguationData":[TD([[makeQuery(id+"F45.imprint","IMPRINT",EDGE,{"derivedFrom":sQuery(id+"F45.wireOp",EDGE,"E194.0")}),-1.0]])]});
            extrude(context, id + "F47", {"entities" : qUnion([Q0, Q1]), "oppositeDirection" : true, "depth" : 10 * mm, "offsetDistance" : 25 * mm, "hasSecondDirection" : true, "secondDirectionOppositeDirection" : false, "secondDirectionDepth" : 5 * mm});
        }
        {
            var Q0;
            Q0=makeQuery(id+"F45.imprint","IMPRINT",FACE,{"disambiguationData":[TD([[makeQuery(id+"F45.imprint","IMPRINT",EDGE,{"derivedFrom":sQuery(id+"F45.wireOp",EDGE,"E194.0")}),-1.0]])]});
            extrude(context, id + "F48", {"entities" : qUnion([Q0]), "operationType" : NewBodyOperationType.REMOVE, "depth" : 6 * mm, "offsetDistance" : 25 * mm});
        }
        {
            var Q0;
            Q0=makeQuery(id+"F40.opExtrude","SWEPT_BODY",BODY,{"disambiguationData":[OSD([sQuery(id+"F39.wireOp",EDGE,"E151"),sQuery(id+"F39.wireOp",EDGE,"E152"),sQuery(id+"F39.wireOp",EDGE,"E153"),sQuery(id+"F39.wireOp",EDGE,"E154"),sQuery(id+"F39.wireOp",EDGE,"E156"),sQuery(id+"F39.wireOp",EDGE,"E158"),sQuery(id+"F39.wireOp",EDGE,"E159"),sQuery(id+"F39.wireOp",EDGE,"E160"),sQuery(id+"F39.wireOp",EDGE,"E161"),sQuery(id+"F39.wireOp",EDGE,"E162"),sQuery(id+"F39.wireOp",EDGE,"E164.filletArc"),sQuery(id+"F39.wireOp",EDGE,"E169"),sQuery(id+"F39.wireOp",EDGE,"E171"),sQuery(id+"F39.wireOp",EDGE,"E177"),sQuery(id+"F39.wireOp",EDGE,"E178")])]});
            var Q1;
            Q1=qCreatedBy(makeId("Right.planeOp"),FACE);
            mirror(context, id + "F49", {"entities" : qUnion([Q0]), "mirrorPlane" : qUnion([Q1])});
        }
        {
            var Q0;
            Q0=makeQuery(id+"F45.imprint","IMPRINT",FACE,{"disambiguationData":[TD([[makeQuery(id+"F45.imprint","IMPRINT",EDGE,{"derivedFrom":sQuery(id+"F45.wireOp",EDGE,"E198.bottom")}),-1.0]])]});
            var Q1;
            Q1=makeQuery(id+"F45.imprint","IMPRINT",FACE,{"disambiguationData":[TD([[makeQuery(id+"F45.imprint","IMPRINT",EDGE,{"derivedFrom":sQuery(id+"F45.wireOp",EDGE,"E197.top")}),1.0]])]});
            extrude(context, id + "F50", {"entities" : qUnion([Q0, Q1]), "operationType" : NewBodyOperationType.ADD, "depth" : 2 * mm, "offsetDistance" : 25 * mm});
        }
        {
            var Q0;
            Q0=makeQuery(id+"F50.opExtrude","CAP_EDGE",EDGE,{"disambiguationData":[OSD([sQuery(id+"F45.wireOp",EDGE,"E197.left")])],"isStart":false});
            var Q1;
            Q1=makeQuery(id+"F50.opExtrude","CAP_EDGE",EDGE,{"disambiguationData":[OSD([sQuery(id+"F45.wireOp",EDGE,"E198.left")])],"isStart":false});
            var Q2;
            Q2=makeQuery(id+"F50.opExtrude","CAP_EDGE",EDGE,{"disambiguationData":[OSD([sQuery(id+"F45.wireOp",EDGE,"E197.right")])],"isStart":false});
            var Q3;
            Q3=makeQuery(id+"F50.opExtrude","CAP_EDGE",EDGE,{"disambiguationData":[OSD([sQuery(id+"F45.wireOp",EDGE,"E198.right")])],"isStart":false});
            chamfer(context, id + "F51", {"entities" : qUnion([Q0, Q1, Q2, Q3]), "width" : 2 * mm, "tangentPropagation" : true});
        }
        {
            var Q0;
            Q0=makeQuery(id+"F46.opExtrude","SWEPT_BODY",BODY,{"disambiguationData":[OSD([sQuery(id+"F45.wireOp",EDGE,"E196")])]});
            var Q1;
            Q1=makeQuery(id+"F47.opExtrude","SWEPT_BODY",BODY,{"disambiguationData":[OSD([sQuery(id+"F45.wireOp",EDGE,"E195")])]});
            var Q2;
            Q2=qCreatedBy(makeId("Right.planeOp"),FACE);
            mirror(context, id + "F52", {"entities" : qUnion([Q0, Q1]), "mirrorPlane" : qUnion([Q2])});
        }
        {
            var Q0;
            Q0=makeQuery(id+"F46.opExtrude","SWEPT_BODY",BODY,{"disambiguationData":[OSD([sQuery(id+"F45.wireOp",EDGE,"E196"),sQuery(id+"F45.wireOp",EDGE,"E197.bottom"),sQuery(id+"F45.wireOp",EDGE,"E198.top")])]});
            var Q1;
            Q1=makeQuery(id+"F47.opExtrude","SWEPT_BODY",BODY,{"disambiguationData":[OSD([sQuery(id+"F45.wireOp",EDGE,"E195")])]});
            var Q2;
            Q2=makeQuery(id+"F52.opPattern","COPY",BODY,{"derivedFrom":makeQuery(id+"F46.opExtrude","SWEPT_BODY",BODY,{"disambiguationData":[OSD([sQuery(id+"F45.wireOp",EDGE,"E196")])]}),"instanceName":"1"});
            var Q3;
            Q3=makeQuery(id+"F52.opPattern","COPY",BODY,{"derivedFrom":makeQuery(id+"F47.opExtrude","SWEPT_BODY",BODY,{"disambiguationData":[OSD([sQuery(id+"F45.wireOp",EDGE,"E195")])]}),"instanceName":"1"});
            var Q4;
            Q4=makeQuery(id+"F21.opExtrude","SWEPT_BODY",BODY,{"disambiguationData":[OSD([sQuery(id+"F20.wireOp",EDGE,"E96.bottom"),sQuery(id+"F20.wireOp",EDGE,"E96.top"),sQuery(id+"F20.wireOp",EDGE,"E96.left"),sQuery(id+"F20.wireOp",EDGE,"E96.right")])]});
            booleanBodies(context, id + "F53", {"operationType" : BooleanOperationType.SUBTRACTION, "tools" : qUnion([Q0, Q1, Q2, Q3]), "targets" : qUnion([Q4])});
        }
        {
            var Q0;
            Q0=makeQuery(id+"F36.boolean.opBoolean","COPY",EDGE,{"derivedFrom":makeQuery(id+"F36.opExtrude","CAP_EDGE",EDGE,{"disambiguationData":[OSD([sQuery(id+"F35.wireOp",EDGE,"E132")])],"isStart":true})});
            var Q1;
            Q1=makeQuery(id+"F36.boolean.opBoolean","COPY",EDGE,{"derivedFrom":makeQuery(id+"F36.opExtrude","CAP_EDGE",EDGE,{"disambiguationData":[OSD([sQuery(id+"F35.wireOp",EDGE,"E133")])],"isStart":true})});
            var Q2;
            Q2=makeQuery(id+"F53.opBoolean","INTERSECT",EDGE,{"derivedFrom":[makeQuery(id+"F21.opExtrude","CAP_FACE",FACE,{"disambiguationData":[OSD([sQuery(id+"F20.wireOp",EDGE,"E96.bottom"),sQuery(id+"F20.wireOp",EDGE,"E96.top"),sQuery(id+"F20.wireOp",EDGE,"E96.left"),sQuery(id+"F20.wireOp",EDGE,"E96.right")])],"isStart":false}),makeQuery(id+"F47.opExtrude","SWEPT_FACE",FACE,{"disambiguationData":[OSD([sQuery(id+"F45.wireOp",EDGE,"E195")])]})]});
            var Q3;
            Q3=makeQuery(id+"F53.opBoolean","INTERSECT",EDGE,{"derivedFrom":[makeQuery(id+"F21.opExtrude","CAP_FACE",FACE,{"disambiguationData":[OSD([sQuery(id+"F20.wireOp",EDGE,"E96.bottom"),sQuery(id+"F20.wireOp",EDGE,"E96.top"),sQuery(id+"F20.wireOp",EDGE,"E96.left"),sQuery(id+"F20.wireOp",EDGE,"E96.right")])],"isStart":false}),makeQuery(id+"F52.opPattern","COPY",FACE,{"derivedFrom":makeQuery(id+"F47.opExtrude","SWEPT_FACE",FACE,{"disambiguationData":[OSD([sQuery(id+"F45.wireOp",EDGE,"E195")])]}),"instanceName":"1"})]});
            var Q4;
            Q4=makeQuery(id+"F36.boolean.opBoolean","COPY",EDGE,{"derivedFrom":makeQuery(id+"F36.opExtrude","CAP_EDGE",EDGE,{"disambiguationData":[OSD([sQuery(id+"F35.wireOp",EDGE,"E140")])],"isStart":true})});
            var Q5;
            Q5=makeQuery(id+"F36.boolean.opBoolean","COPY",EDGE,{"derivedFrom":makeQuery(id+"F36.opExtrude","CAP_EDGE",EDGE,{"disambiguationData":[OSD([sQuery(id+"F35.wireOp",EDGE,"E142")])],"isStart":true})});
            var Q6;
            Q6=makeQuery(id+"F36.boolean.opBoolean","COPY",EDGE,{"derivedFrom":makeQuery(id+"F36.opExtrude","CAP_EDGE",EDGE,{"disambiguationData":[OSD([sQuery(id+"F35.wireOp",EDGE,"E145")])],"isStart":true})});
            var Q7;
            Q7=makeQuery(id+"F36.boolean.opBoolean","COPY",EDGE,{"derivedFrom":makeQuery(id+"F36.opExtrude","CAP_EDGE",EDGE,{"disambiguationData":[OSD([sQuery(id+"F35.wireOp",EDGE,"E147")])],"isStart":true})});
            var Q8;
            Q8=makeQuery(id+"F36.boolean.opBoolean","COPY",EDGE,{"derivedFrom":makeQuery(id+"F36.opExtrude","CAP_EDGE",EDGE,{"disambiguationData":[OSD([sQuery(id+"F35.wireOp",EDGE,"E135")])],"isStart":true})});
            var Q9;
            Q9=makeQuery(id+"F36.boolean.opBoolean","COPY",EDGE,{"derivedFrom":makeQuery(id+"F36.opExtrude","CAP_EDGE",EDGE,{"disambiguationData":[OSD([sQuery(id+"F35.wireOp",EDGE,"E134")])],"isStart":true})});
            chamfer(context, id + "F54", {"entities" : qUnion([Q0, Q1, Q2, Q3, Q4, Q5, Q6, Q7, Q8, Q9]), "width" : 1.75 * mm, "tangentPropagation" : true});
        }
    });
